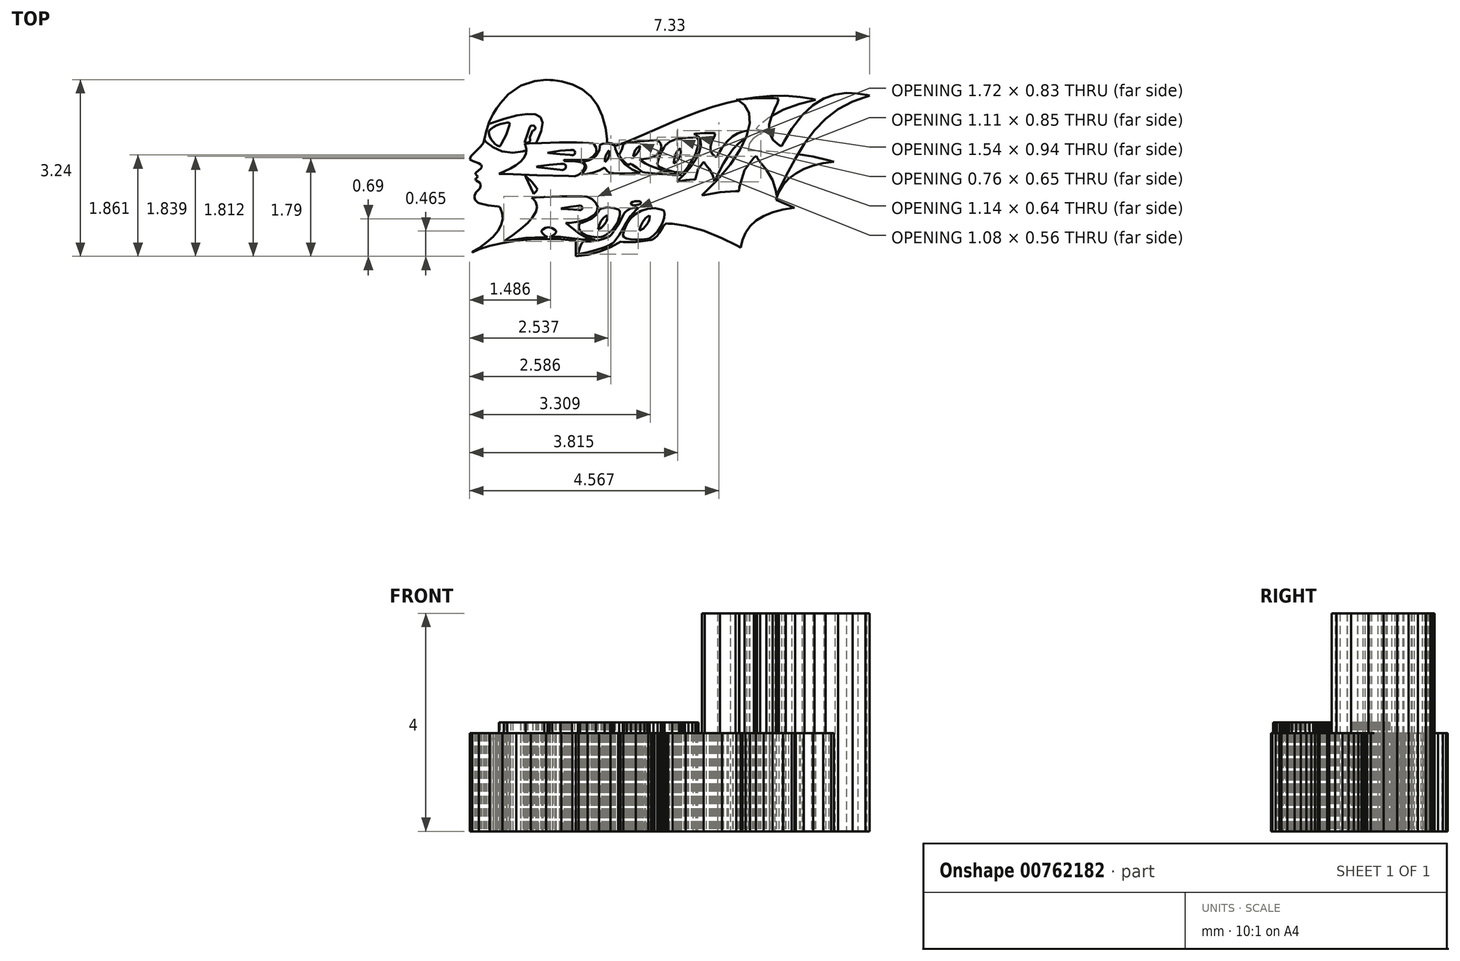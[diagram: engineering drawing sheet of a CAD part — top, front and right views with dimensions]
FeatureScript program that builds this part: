
annotation { "Feature Type Name" : "Feature", "Feature Type Description" : "" }
export const myFeature = defineFeature(function(context is Context, id is Id, definition is map)
    precondition{}
    {
        {
            var Q0;
            Q0=qCreatedBy(makeId("Top.planeOp"),FACE);
            var sketch = newSketch(context, id + "F0", { "sketchPlane" : qUnion([Q0])});
            skLineSegment(sketch, "E0", {"start": v(-3.33, 0.15) * mm, "end": v(-3.34, 0.16) * mm});
            skLineSegment(sketch, "E1", {"start": v(-3.34, 0.16) * mm, "end": v(-3.31, 0.22) * mm});
            skLineSegment(sketch, "E2", {"start": v(-3.31, 0.22) * mm, "end": v(-3.23, 0.3) * mm});
            skLineSegment(sketch, "E3", {"start": v(-3.23, 0.3) * mm, "end": v(-3.14, 0.4) * mm});
            skLineSegment(sketch, "E4", {"start": v(-3.14, 0.4) * mm, "end": v(-3.09, 0.46) * mm});
            skLineSegment(sketch, "E5", {"start": v(-3.09, 0.46) * mm, "end": v(-3.08, 0.48) * mm});
            skLineSegment(sketch, "E6", {"start": v(-3.08, 0.48) * mm, "end": v(-3.07, 0.53) * mm});
            skLineSegment(sketch, "E7", {"start": v(-3.07, 0.53) * mm, "end": v(-3.04, 0.67) * mm});
            skLineSegment(sketch, "E8", {"start": v(-3.04, 0.67) * mm, "end": v(-2.99, 0.84) * mm});
            skLineSegment(sketch, "E9", {"start": v(-2.99, 0.84) * mm, "end": v(-2.91, 1) * mm});
            skLineSegment(sketch, "E10", {"start": v(-2.91, 1) * mm, "end": v(-2.85, 1.1) * mm});
            skLineSegment(sketch, "E11", {"start": v(-2.85, 1.1) * mm, "end": v(-2.82, 1.12) * mm});
            skLineSegment(sketch, "E12", {"start": v(-2.82, 1.12) * mm, "end": v(-2.78, 1.19) * mm});
            skLineSegment(sketch, "E13", {"start": v(-2.78, 1.19) * mm, "end": v(-2.63, 1.35) * mm});
            skLineSegment(sketch, "E14", {"start": v(-2.63, 1.35) * mm, "end": v(-2.4, 1.51) * mm});
            skLineSegment(sketch, "E15", {"start": v(-2.4, 1.51) * mm, "end": v(-2.15, 1.6) * mm});
            skLineSegment(sketch, "E16", {"start": v(-2.15, 1.6) * mm, "end": v(-1.94, 1.62) * mm});
            skLineSegment(sketch, "E17", {"start": v(-1.94, 1.62) * mm, "end": v(-1.87, 1.61) * mm});
            skLineSegment(sketch, "E18", {"start": v(-1.87, 1.61) * mm, "end": v(-1.81, 1.61) * mm});
            skLineSegment(sketch, "E19", {"start": v(-1.81, 1.61) * mm, "end": v(-1.65, 1.6) * mm});
            skLineSegment(sketch, "E20", {"start": v(-1.65, 1.6) * mm, "end": v(-1.45, 1.53) * mm});
            skLineSegment(sketch, "E21", {"start": v(-1.45, 1.53) * mm, "end": v(-1.27, 1.44) * mm});
            skLineSegment(sketch, "E22", {"start": v(-1.27, 1.44) * mm, "end": v(-1.12, 1.32) * mm});
            skLineSegment(sketch, "E23", {"start": v(-1.12, 1.32) * mm, "end": v(-1, 1.15) * mm});
            skLineSegment(sketch, "E24", {"start": v(-1, 1.15) * mm, "end": v(-0.9, 0.96) * mm});
            skLineSegment(sketch, "E25", {"start": v(-0.9, 0.96) * mm, "end": v(-0.85, 0.73) * mm});
            skLineSegment(sketch, "E26", {"start": v(-0.85, 0.73) * mm, "end": v(-0.82, 0.53) * mm});
            skLineSegment(sketch, "E27", {"start": v(-0.82, 0.53) * mm, "end": v(-0.82, 0.46) * mm});
            skLineSegment(sketch, "E28", {"start": v(-0.82, 0.46) * mm, "end": v(-0.8, 0.47) * mm});
            skLineSegment(sketch, "E29", {"start": v(-0.8, 0.47) * mm, "end": v(-0.73, 0.45) * mm});
            skLineSegment(sketch, "E30", {"start": v(-0.73, 0.45) * mm, "end": v(-0.68, 0.42) * mm});
            skLineSegment(sketch, "E31", {"start": v(-0.68, 0.42) * mm, "end": v(-0.67, 0.4) * mm});
            skLineSegment(sketch, "E32", {"start": v(-0.67, 0.4) * mm, "end": v(-0.63, 0.42) * mm});
            skLineSegment(sketch, "E33", {"start": v(-0.63, 0.42) * mm, "end": v(-0.52, 0.46) * mm});
            skLineSegment(sketch, "E34", {"start": v(-0.52, 0.46) * mm, "end": v(-0.36, 0.52) * mm});
            skLineSegment(sketch, "E35", {"start": v(-0.36, 0.52) * mm, "end": v(-0.19, 0.6) * mm});
            skLineSegment(sketch, "E36", {"start": v(-0.19, 0.6) * mm, "end": v(0, 0.68) * mm});
            skLineSegment(sketch, "E37", {"start": v(0, 0.68) * mm, "end": v(0.2, 0.77) * mm});
            skLineSegment(sketch, "E38", {"start": v(0.2, 0.77) * mm, "end": v(0.42, 0.86) * mm});
            skLineSegment(sketch, "E39", {"start": v(0.42, 0.86) * mm, "end": v(0.64, 0.95) * mm});
            skLineSegment(sketch, "E40", {"start": v(0.64, 0.95) * mm, "end": v(0.88, 1.04) * mm});
            skLineSegment(sketch, "E41", {"start": v(0.88, 1.04) * mm, "end": v(1.12, 1.12) * mm});
            skLineSegment(sketch, "E42", {"start": v(1.12, 1.12) * mm, "end": v(1.37, 1.2) * mm});
            skLineSegment(sketch, "E43", {"start": v(1.37, 1.2) * mm, "end": v(1.63, 1.25) * mm});
            skLineSegment(sketch, "E44", {"start": v(1.63, 1.25) * mm, "end": v(1.9, 1.3) * mm});
            skLineSegment(sketch, "E45", {"start": v(1.9, 1.3) * mm, "end": v(2.17, 1.32) * mm});
            skLineSegment(sketch, "E46", {"start": v(2.17, 1.32) * mm, "end": v(2.44, 1.33) * mm});
            skLineSegment(sketch, "E47", {"start": v(2.44, 1.33) * mm, "end": v(2.72, 1.3) * mm});
            skLineSegment(sketch, "E48", {"start": v(2.72, 1.3) * mm, "end": v(2.93, 1.27) * mm});
            skLineSegment(sketch, "E49", {"start": v(2.93, 1.27) * mm, "end": v(3, 1.25) * mm});
            skLineSegment(sketch, "E50", {"start": v(3, 1.25) * mm, "end": v(2.92, 1.23) * mm});
            skLineSegment(sketch, "E51", {"start": v(2.92, 1.23) * mm, "end": v(2.7, 1.18) * mm});
            skLineSegment(sketch, "E52", {"start": v(2.7, 1.18) * mm, "end": v(2.42, 1.07) * mm});
            skLineSegment(sketch, "E53", {"start": v(2.42, 1.07) * mm, "end": v(2.15, 0.93) * mm});
            skLineSegment(sketch, "E54", {"start": v(2.15, 0.93) * mm, "end": v(1.96, 0.77) * mm});
            skLineSegment(sketch, "E55", {"start": v(1.96, 0.77) * mm, "end": v(1.9, 0.72) * mm});
            skLineSegment(sketch, "E56", {"start": v(1.9, 0.72) * mm, "end": v(2.08, 0.68) * mm});
            skLineSegment(sketch, "E57", {"start": v(2.08, 0.68) * mm, "end": v(2.05, 0.66) * mm});
            skLineSegment(sketch, "E58", {"start": v(2.05, 0.66) * mm, "end": v(1.95, 0.6) * mm});
            skLineSegment(sketch, "E59", {"start": v(1.95, 0.6) * mm, "end": v(1.85, 0.54) * mm});
            skLineSegment(sketch, "E60", {"start": v(1.85, 0.54) * mm, "end": v(1.79, 0.45) * mm});
            skLineSegment(sketch, "E61", {"start": v(1.79, 0.45) * mm, "end": v(1.77, 0.36) * mm});
            skLineSegment(sketch, "E62", {"start": v(1.77, 0.36) * mm, "end": v(1.77, 0.32) * mm});
            skLineSegment(sketch, "E63", {"start": v(1.77, 0.32) * mm, "end": v(1.86, 0.32) * mm});
            skLineSegment(sketch, "E64", {"start": v(1.86, 0.32) * mm, "end": v(2.16, 0.31) * mm});
            skLineSegment(sketch, "E65", {"start": v(2.16, 0.31) * mm, "end": v(2.56, 0.27) * mm});
            skLineSegment(sketch, "E66", {"start": v(2.56, 0.27) * mm, "end": v(2.96, 0.2) * mm});
            skLineSegment(sketch, "E67", {"start": v(2.96, 0.2) * mm, "end": v(3.24, 0.14) * mm});
            skLineSegment(sketch, "E68", {"start": v(3.24, 0.14) * mm, "end": v(3.34, 0.11) * mm});
            skLineSegment(sketch, "E69", {"start": v(3.34, 0.11) * mm, "end": v(3.29, 0.1) * mm});
            skLineSegment(sketch, "E70", {"start": v(3.29, 0.1) * mm, "end": v(3.14, 0.09) * mm});
            skLineSegment(sketch, "E71", {"start": v(3.14, 0.09) * mm, "end": v(2.95, 0.04) * mm});
            skLineSegment(sketch, "E72", {"start": v(2.95, 0.04) * mm, "end": v(2.79, -0.02) * mm});
            skLineSegment(sketch, "E73", {"start": v(2.79, -0.02) * mm, "end": v(2.64, -0.1) * mm});
            skLineSegment(sketch, "E74", {"start": v(2.64, -0.1) * mm, "end": v(2.5, -0.2) * mm});
            skLineSegment(sketch, "E75", {"start": v(2.5, -0.2) * mm, "end": v(2.4, -0.31) * mm});
            skLineSegment(sketch, "E76", {"start": v(2.4, -0.31) * mm, "end": v(2.33, -0.44) * mm});
            skLineSegment(sketch, "E77", {"start": v(2.33, -0.44) * mm, "end": v(2.29, -0.55) * mm});
            skLineSegment(sketch, "E78", {"start": v(2.29, -0.55) * mm, "end": v(2.28, -0.59) * mm});
            skLineSegment(sketch, "E79", {"start": v(2.28, -0.59) * mm, "end": v(2.62, -0.73) * mm});
            skLineSegment(sketch, "E80", {"start": v(2.62, -0.73) * mm, "end": v(2.56, -0.74) * mm});
            skLineSegment(sketch, "E81", {"start": v(2.56, -0.74) * mm, "end": v(2.4, -0.76) * mm});
            skLineSegment(sketch, "E82", {"start": v(2.4, -0.76) * mm, "end": v(2.21, -0.81) * mm});
            skLineSegment(sketch, "E83", {"start": v(2.21, -0.81) * mm, "end": v(2.05, -0.88) * mm});
            skLineSegment(sketch, "E84", {"start": v(2.05, -0.88) * mm, "end": v(1.91, -0.97) * mm});
            skLineSegment(sketch, "E85", {"start": v(1.91, -0.97) * mm, "end": v(1.8, -1.07) * mm});
            skLineSegment(sketch, "E86", {"start": v(1.8, -1.07) * mm, "end": v(1.71, -1.19) * mm});
            skLineSegment(sketch, "E87", {"start": v(1.71, -1.19) * mm, "end": v(1.66, -1.32) * mm});
            skLineSegment(sketch, "E88", {"start": v(1.66, -1.32) * mm, "end": v(1.63, -1.43) * mm});
            skLineSegment(sketch, "E89", {"start": v(1.63, -1.43) * mm, "end": v(1.63, -1.46) * mm});
            skLineSegment(sketch, "E90", {"start": v(1.63, -1.46) * mm, "end": v(1.54, -1.42) * mm});
            skLineSegment(sketch, "E91", {"start": v(1.54, -1.42) * mm, "end": v(1.29, -1.29) * mm});
            skLineSegment(sketch, "E92", {"start": v(1.29, -1.29) * mm, "end": v(0.95, -1.15) * mm});
            skLineSegment(sketch, "E93", {"start": v(0.95, -1.15) * mm, "end": v(0.62, -1.06) * mm});
            skLineSegment(sketch, "E94", {"start": v(0.62, -1.06) * mm, "end": v(0.38, -1.02) * mm});
            skLineSegment(sketch, "E95", {"start": v(0.38, -1.02) * mm, "end": v(0.3, -1.02) * mm});
            skLineSegment(sketch, "E96", {"start": v(0.3, -1.02) * mm, "end": v(0.29, -1.02) * mm});
            skLineSegment(sketch, "E97", {"start": v(0.29, -1.02) * mm, "end": v(0.26, -1.02) * mm});
            skLineSegment(sketch, "E98", {"start": v(0.26, -1.02) * mm, "end": v(0.23, -1.05) * mm});
            skLineSegment(sketch, "E99", {"start": v(0.23, -1.05) * mm, "end": v(0.2, -1.09) * mm});
            skLineSegment(sketch, "E100", {"start": v(0.2, -1.09) * mm, "end": v(0.17, -1.14) * mm});
            skLineSegment(sketch, "E101", {"start": v(0.17, -1.14) * mm, "end": v(0.14, -1.19) * mm});
            skLineSegment(sketch, "E102", {"start": v(0.14, -1.19) * mm, "end": v(0.1, -1.24) * mm});
            skLineSegment(sketch, "E103", {"start": v(0.1, -1.24) * mm, "end": v(0.05, -1.29) * mm});
            skLineSegment(sketch, "E104", {"start": v(0.05, -1.29) * mm, "end": v(0, -1.31) * mm});
            skLineSegment(sketch, "E105", {"start": v(0, -1.31) * mm, "end": v(-0.01, -1.32) * mm});
            skLineSegment(sketch, "E106", {"start": v(-0.01, -1.32) * mm, "end": v(-0.07, -1.33) * mm});
            skLineSegment(sketch, "E107", {"start": v(-0.07, -1.33) * mm, "end": v(-0.3, -1.36) * mm});
            skLineSegment(sketch, "E108", {"start": v(-0.3, -1.36) * mm, "end": v(-0.52, -1.36) * mm});
            skLineSegment(sketch, "E109", {"start": v(-0.52, -1.36) * mm, "end": v(-0.57, -1.35) * mm});
            skLineSegment(sketch, "E110", {"start": v(-0.57, -1.35) * mm, "end": v(-0.62, -1.38) * mm});
            skLineSegment(sketch, "E111", {"start": v(-0.62, -1.38) * mm, "end": v(-0.76, -1.45) * mm});
            skLineSegment(sketch, "E112", {"start": v(-0.76, -1.45) * mm, "end": v(-0.97, -1.53) * mm});
            skLineSegment(sketch, "E113", {"start": v(-0.97, -1.53) * mm, "end": v(-1.18, -1.6) * mm});
            skLineSegment(sketch, "E114", {"start": v(-1.18, -1.6) * mm, "end": v(-1.34, -1.62) * mm});
            skLineSegment(sketch, "E115", {"start": v(-1.34, -1.62) * mm, "end": v(-1.4, -1.62) * mm});
            skLineSegment(sketch, "E116", {"start": v(-1.4, -1.62) * mm, "end": v(-1.4, -1.34) * mm});
            skLineSegment(sketch, "E117", {"start": v(-1.4, -1.34) * mm, "end": v(-1.46, -1.33) * mm});
            skLineSegment(sketch, "E118", {"start": v(-1.46, -1.33) * mm, "end": v(-1.66, -1.3) * mm});
            skLineSegment(sketch, "E119", {"start": v(-1.66, -1.3) * mm, "end": v(-1.94, -1.3) * mm});
            skLineSegment(sketch, "E120", {"start": v(-1.94, -1.3) * mm, "end": v(-2.22, -1.3) * mm});
            skLineSegment(sketch, "E121", {"start": v(-2.22, -1.3) * mm, "end": v(-2.49, -1.33) * mm});
            skLineSegment(sketch, "E122", {"start": v(-2.49, -1.33) * mm, "end": v(-2.74, -1.38) * mm});
            skLineSegment(sketch, "E123", {"start": v(-2.74, -1.38) * mm, "end": v(-2.97, -1.43) * mm});
            skLineSegment(sketch, "E124", {"start": v(-2.97, -1.43) * mm, "end": v(-3.17, -1.5) * mm});
            skLineSegment(sketch, "E125", {"start": v(-3.17, -1.5) * mm, "end": v(-3.3, -1.55) * mm});
            skLineSegment(sketch, "E126", {"start": v(-3.3, -1.55) * mm, "end": v(-3.33, -1.57) * mm});
            skLineSegment(sketch, "E127", {"start": v(-3.33, -1.57) * mm, "end": v(-3.3, -1.55) * mm});
            skLineSegment(sketch, "E128", {"start": v(-3.3, -1.55) * mm, "end": v(-3.17, -1.47) * mm});
            skLineSegment(sketch, "E129", {"start": v(-3.17, -1.47) * mm, "end": v(-3.03, -1.37) * mm});
            skLineSegment(sketch, "E130", {"start": v(-3.03, -1.37) * mm, "end": v(-2.91, -1.26) * mm});
            skLineSegment(sketch, "E131", {"start": v(-2.91, -1.26) * mm, "end": v(-2.82, -1.15) * mm});
            skLineSegment(sketch, "E132", {"start": v(-2.82, -1.15) * mm, "end": v(-2.76, -1.05) * mm});
            skLineSegment(sketch, "E133", {"start": v(-2.76, -1.05) * mm, "end": v(-2.74, -0.93) * mm});
            skLineSegment(sketch, "E134", {"start": v(-2.74, -0.93) * mm, "end": v(-2.75, -0.82) * mm});
            skLineSegment(sketch, "E135", {"start": v(-2.75, -0.82) * mm, "end": v(-2.78, -0.74) * mm});
            skLineSegment(sketch, "E136", {"start": v(-2.78, -0.74) * mm, "end": v(-2.8, -0.7) * mm});
            skLineSegment(sketch, "E137", {"start": v(-2.8, -0.7) * mm, "end": v(-2.83, -0.7) * mm});
            skLineSegment(sketch, "E138", {"start": v(-2.83, -0.7) * mm, "end": v(-3, -0.69) * mm});
            skLineSegment(sketch, "E139", {"start": v(-3, -0.69) * mm, "end": v(-3.16, -0.65) * mm});
            skLineSegment(sketch, "E140", {"start": v(-3.16, -0.65) * mm, "end": v(-3.2, -0.63) * mm});
            skLineSegment(sketch, "E141", {"start": v(-3.2, -0.63) * mm, "end": v(-3.2, -0.62) * mm});
            skLineSegment(sketch, "E142", {"start": v(-3.2, -0.62) * mm, "end": v(-3.24, -0.58) * mm});
            skLineSegment(sketch, "E143", {"start": v(-3.24, -0.58) * mm, "end": v(-3.25, -0.52) * mm});
            skLineSegment(sketch, "E144", {"start": v(-3.25, -0.52) * mm, "end": v(-3.23, -0.45) * mm});
            skLineSegment(sketch, "E145", {"start": v(-3.23, -0.45) * mm, "end": v(-3.18, -0.4) * mm});
            skLineSegment(sketch, "E146", {"start": v(-3.18, -0.4) * mm, "end": v(-3.16, -0.38) * mm});
            skLineSegment(sketch, "E147", {"start": v(-3.16, -0.38) * mm, "end": v(-3.16, -0.37) * mm});
            skLineSegment(sketch, "E148", {"start": v(-3.16, -0.37) * mm, "end": v(-3.14, -0.33) * mm});
            skLineSegment(sketch, "E149", {"start": v(-3.14, -0.33) * mm, "end": v(-3.15, -0.28) * mm});
            skLineSegment(sketch, "E150", {"start": v(-3.15, -0.28) * mm, "end": v(-3.15, -0.27) * mm});
            skLineSegment(sketch, "E151", {"start": v(-3.15, -0.27) * mm, "end": v(-3.16, -0.27) * mm});
            skLineSegment(sketch, "E152", {"start": v(-3.16, -0.27) * mm, "end": v(-3.22, -0.23) * mm});
            skLineSegment(sketch, "E153", {"start": v(-3.22, -0.23) * mm, "end": v(-3.23, -0.23) * mm});
            skLineSegment(sketch, "E154", {"start": v(-3.23, -0.23) * mm, "end": v(-3.23, -0.22) * mm});
            skLineSegment(sketch, "E155", {"start": v(-3.23, -0.22) * mm, "end": v(-3.24, -0.2) * mm});
            skLineSegment(sketch, "E156", {"start": v(-3.24, -0.2) * mm, "end": v(-3.23, -0.2) * mm});
            skLineSegment(sketch, "E157", {"start": v(-3.23, -0.2) * mm, "end": v(-3.23, -0.19) * mm});
            skLineSegment(sketch, "E158", {"start": v(-3.23, -0.19) * mm, "end": v(-3.22, -0.19) * mm});
            skLineSegment(sketch, "E159", {"start": v(-3.22, -0.19) * mm, "end": v(-3.2, -0.18) * mm});
            skLineSegment(sketch, "E160", {"start": v(-3.2, -0.18) * mm, "end": v(-3.2, -0.16) * mm});
            skLineSegment(sketch, "E161", {"start": v(-3.2, -0.16) * mm, "end": v(-3.2, -0.14) * mm});
            skLineSegment(sketch, "E162", {"start": v(-3.2, -0.14) * mm, "end": v(-3.22, -0.12) * mm});
            skLineSegment(sketch, "E163", {"start": v(-3.22, -0.12) * mm, "end": v(-3.23, -0.12) * mm});
            skLineSegment(sketch, "E164", {"start": v(-3.23, -0.12) * mm, "end": v(-3.23, -0.12) * mm});
            skLineSegment(sketch, "E165", {"start": v(-3.23, -0.12) * mm, "end": v(-3.23, -0.1) * mm});
            skLineSegment(sketch, "E166", {"start": v(-3.23, -0.1) * mm, "end": v(-3.23, -0.09) * mm});
            skLineSegment(sketch, "E167", {"start": v(-3.23, -0.09) * mm, "end": v(-3.14, 0) * mm});
            skLineSegment(sketch, "E168", {"start": v(-3.14, 0) * mm, "end": v(-3.13, 0) * mm});
            skLineSegment(sketch, "E169", {"start": v(-3.13, 0) * mm, "end": v(-3.12, 0.01) * mm});
            skLineSegment(sketch, "E170", {"start": v(-3.12, 0.01) * mm, "end": v(-3.12, 0.04) * mm});
            skLineSegment(sketch, "E171", {"start": v(-3.12, 0.04) * mm, "end": v(-3.13, 0.05) * mm});
            skLineSegment(sketch, "E172", {"start": v(-3.13, 0.05) * mm, "end": v(-3.13, 0.06) * mm});
            skLineSegment(sketch, "E173", {"start": v(-3.13, 0.06) * mm, "end": v(-3.13, 0.06) * mm});
            skLineSegment(sketch, "E174", {"start": v(-3.13, 0.06) * mm, "end": v(-3.14, 0.07) * mm});
            skLineSegment(sketch, "E175", {"start": v(-3.14, 0.07) * mm, "end": v(-3.18, 0.1) * mm});
            skLineSegment(sketch, "E176", {"start": v(-3.18, 0.1) * mm, "end": v(-3.23, 0.11) * mm});
            skLineSegment(sketch, "E177", {"start": v(-3.23, 0.11) * mm, "end": v(-3.28, 0.13) * mm});
            skLineSegment(sketch, "E178", {"start": v(-3.28, 0.13) * mm, "end": v(-3.32, 0.15) * mm});
            skLineSegment(sketch, "E179", {"start": v(-3.32, 0.15) * mm, "end": v(-3.33, 0.15) * mm});
            skLineSegment(sketch, "E180", {"start": v(-2.33, 0.45) * mm, "end": v(-2.26, 0.45) * mm});
            skLineSegment(sketch, "E181", {"start": v(-2.26, 0.45) * mm, "end": v(-2.02, 0.46) * mm});
            skLineSegment(sketch, "E182", {"start": v(-2.02, 0.46) * mm, "end": v(-1.7, 0.47) * mm});
            skLineSegment(sketch, "E183", {"start": v(-1.7, 0.47) * mm, "end": v(-1.38, 0.47) * mm});
            skLineSegment(sketch, "E184", {"start": v(-1.38, 0.47) * mm, "end": v(-1.15, 0.46) * mm});
            skLineSegment(sketch, "E185", {"start": v(-1.15, 0.46) * mm, "end": v(-1.07, 0.45) * mm});
            skLineSegment(sketch, "E186", {"start": v(-1.07, 0.45) * mm, "end": v(-1.06, 0.43) * mm});
            skLineSegment(sketch, "E187", {"start": v(-1.06, 0.43) * mm, "end": v(-1.02, 0.37) * mm});
            skLineSegment(sketch, "E188", {"start": v(-1.02, 0.37) * mm, "end": v(-1.02, 0.29) * mm});
            skLineSegment(sketch, "E189", {"start": v(-1.02, 0.29) * mm, "end": v(-1.07, 0.21) * mm});
            skLineSegment(sketch, "E190", {"start": v(-1.07, 0.21) * mm, "end": v(-1.16, 0.16) * mm});
            skLineSegment(sketch, "E191", {"start": v(-1.16, 0.16) * mm, "end": v(-1.2, 0.15) * mm});
            skLineSegment(sketch, "E192", {"start": v(-1.2, 0.15) * mm, "end": v(-1.23, 0.15) * mm});
            skLineSegment(sketch, "E193", {"start": v(-1.23, 0.15) * mm, "end": v(-1.57, 0.15) * mm});
            skLineSegment(sketch, "E194", {"start": v(-1.57, 0.15) * mm, "end": v(-1.6, 0.15) * mm});
            skLineSegment(sketch, "E195", {"start": v(-1.6, 0.15) * mm, "end": v(-1.6, 0.15) * mm});
            skLineSegment(sketch, "E196", {"start": v(-1.6, 0.15) * mm, "end": v(-1.61, 0.13) * mm});
            skLineSegment(sketch, "E197", {"start": v(-1.61, 0.13) * mm, "end": v(-1.6, 0.13) * mm});
            skLineSegment(sketch, "E198", {"start": v(-1.6, 0.13) * mm, "end": v(-1.6, 0.13) * mm});
            skLineSegment(sketch, "E199", {"start": v(-1.6, 0.13) * mm, "end": v(-1.57, 0.13) * mm});
            skLineSegment(sketch, "E200", {"start": v(-1.57, 0.13) * mm, "end": v(-1.5, 0.13) * mm});
            skLineSegment(sketch, "E201", {"start": v(-1.5, 0.13) * mm, "end": v(-1.4, 0.12) * mm});
            skLineSegment(sketch, "E202", {"start": v(-1.4, 0.12) * mm, "end": v(-1.32, 0.11) * mm});
            skLineSegment(sketch, "E203", {"start": v(-1.32, 0.11) * mm, "end": v(-1.28, 0.1) * mm});
            skLineSegment(sketch, "E204", {"start": v(-1.28, 0.1) * mm, "end": v(-1.27, 0.1) * mm});
            skLineSegment(sketch, "E205", {"start": v(-1.27, 0.1) * mm, "end": v(-1.26, 0.09) * mm});
            skLineSegment(sketch, "E206", {"start": v(-1.26, 0.09) * mm, "end": v(-1.24, 0.07) * mm});
            skLineSegment(sketch, "E207", {"start": v(-1.24, 0.07) * mm, "end": v(-1.23, 0.04) * mm});
            skLineSegment(sketch, "E208", {"start": v(-1.23, 0.04) * mm, "end": v(-1.23, 0) * mm});
            skLineSegment(sketch, "E209", {"start": v(-1.23, 0) * mm, "end": v(-1.25, -0.03) * mm});
            skLineSegment(sketch, "E210", {"start": v(-1.25, -0.03) * mm, "end": v(-1.28, -0.07) * mm});
            skLineSegment(sketch, "E211", {"start": v(-1.28, -0.07) * mm, "end": v(-1.32, -0.1) * mm});
            skLineSegment(sketch, "E212", {"start": v(-1.32, -0.1) * mm, "end": v(-1.36, -0.13) * mm});
            skLineSegment(sketch, "E213", {"start": v(-1.36, -0.13) * mm, "end": v(-1.4, -0.15) * mm});
            skLineSegment(sketch, "E214", {"start": v(-1.4, -0.15) * mm, "end": v(-1.4, -0.15) * mm});
            skLineSegment(sketch, "E215", {"start": v(-1.4, -0.15) * mm, "end": v(-1.53, -0.15) * mm});
            skLineSegment(sketch, "E216", {"start": v(-1.53, -0.15) * mm, "end": v(-2.1, -0.13) * mm});
            skLineSegment(sketch, "E217", {"start": v(-2.1, -0.13) * mm, "end": v(-2.69, -0.1) * mm});
            skLineSegment(sketch, "E218", {"start": v(-2.69, -0.1) * mm, "end": v(-2.8, -0.1) * mm});
            skLineSegment(sketch, "E219", {"start": v(-2.8, -0.1) * mm, "end": v(-2.78, -0.1) * mm});
            skLineSegment(sketch, "E220", {"start": v(-2.78, -0.1) * mm, "end": v(-2.7, -0.06) * mm});
            skLineSegment(sketch, "E221", {"start": v(-2.7, -0.06) * mm, "end": v(-2.59, 0) * mm});
            skLineSegment(sketch, "E222", {"start": v(-2.59, 0) * mm, "end": v(-2.5, 0.05) * mm});
            skLineSegment(sketch, "E223", {"start": v(-2.5, 0.05) * mm, "end": v(-2.4, 0.12) * mm});
            skLineSegment(sketch, "E224", {"start": v(-2.4, 0.12) * mm, "end": v(-2.34, 0.19) * mm});
            skLineSegment(sketch, "E225", {"start": v(-2.34, 0.19) * mm, "end": v(-2.3, 0.27) * mm});
            skLineSegment(sketch, "E226", {"start": v(-2.3, 0.27) * mm, "end": v(-2.3, 0.35) * mm});
            skLineSegment(sketch, "E227", {"start": v(-2.3, 0.35) * mm, "end": v(-2.32, 0.43) * mm});
            skLineSegment(sketch, "E228", {"start": v(-2.32, 0.43) * mm, "end": v(-2.33, 0.45) * mm});
            skLineSegment(sketch, "E229", {"start": v(-1.91, 0.28) * mm, "end": v(-1.88, 0.29) * mm});
            skLineSegment(sketch, "E230", {"start": v(-1.88, 0.29) * mm, "end": v(-1.68, 0.32) * mm});
            skLineSegment(sketch, "E231", {"start": v(-1.68, 0.32) * mm, "end": v(-1.49, 0.33) * mm});
            skLineSegment(sketch, "E232", {"start": v(-1.49, 0.33) * mm, "end": v(-1.45, 0.33) * mm});
            skLineSegment(sketch, "E233", {"start": v(-1.45, 0.33) * mm, "end": v(-1.44, 0.33) * mm});
            skLineSegment(sketch, "E234", {"start": v(-1.44, 0.33) * mm, "end": v(-1.42, 0.32) * mm});
            skLineSegment(sketch, "E235", {"start": v(-1.42, 0.32) * mm, "end": v(-1.4, 0.28) * mm});
            skLineSegment(sketch, "E236", {"start": v(-1.4, 0.28) * mm, "end": v(-1.42, 0.25) * mm});
            skLineSegment(sketch, "E237", {"start": v(-1.42, 0.25) * mm, "end": v(-1.45, 0.24) * mm});
            skLineSegment(sketch, "E238", {"start": v(-1.45, 0.24) * mm, "end": v(-1.46, 0.24) * mm});
            skLineSegment(sketch, "E239", {"start": v(-1.46, 0.24) * mm, "end": v(-1.5, 0.24) * mm});
            skLineSegment(sketch, "E240", {"start": v(-1.5, 0.24) * mm, "end": v(-1.69, 0.25) * mm});
            skLineSegment(sketch, "E241", {"start": v(-1.69, 0.25) * mm, "end": v(-1.87, 0.27) * mm});
            skLineSegment(sketch, "E242", {"start": v(-1.87, 0.27) * mm, "end": v(-1.91, 0.28) * mm});
            skLineSegment(sketch, "E243", {"start": v(-1.26, 0.12) * mm, "end": v(-1.25, 0.11) * mm});
            skLineSegment(sketch, "E244", {"start": v(-1.25, 0.11) * mm, "end": v(-1.22, 0.07) * mm});
            skLineSegment(sketch, "E245", {"start": v(-1.22, 0.07) * mm, "end": v(-1.2, 0.02) * mm});
            skLineSegment(sketch, "E246", {"start": v(-1.2, 0.02) * mm, "end": v(-1.23, -0.04) * mm});
            skLineSegment(sketch, "E247", {"start": v(-1.23, -0.04) * mm, "end": v(-1.27, -0.1) * mm});
            skLineSegment(sketch, "E248", {"start": v(-1.27, -0.1) * mm, "end": v(-1.3, -0.11) * mm});
            skLineSegment(sketch, "E249", {"start": v(-1.3, -0.11) * mm, "end": v(-1.26, -0.11) * mm});
            skLineSegment(sketch, "E250", {"start": v(-1.26, -0.11) * mm, "end": v(-1.18, -0.1) * mm});
            skLineSegment(sketch, "E251", {"start": v(-1.18, -0.1) * mm, "end": v(-1.07, -0.08) * mm});
            skLineSegment(sketch, "E252", {"start": v(-1.07, -0.08) * mm, "end": v(-0.96, -0.04) * mm});
            skLineSegment(sketch, "E253", {"start": v(-0.96, -0.04) * mm, "end": v(-0.89, 0) * mm});
            skLineSegment(sketch, "E254", {"start": v(-0.89, 0) * mm, "end": v(-0.87, 0.01) * mm});
            skLineSegment(sketch, "E255", {"start": v(-0.87, 0.01) * mm, "end": v(-0.86, 0) * mm});
            skLineSegment(sketch, "E256", {"start": v(-0.86, 0) * mm, "end": v(-0.84, -0.03) * mm});
            skLineSegment(sketch, "E257", {"start": v(-0.84, -0.03) * mm, "end": v(-0.82, -0.06) * mm});
            skLineSegment(sketch, "E258", {"start": v(-0.82, -0.06) * mm, "end": v(-0.78, -0.08) * mm});
            skLineSegment(sketch, "E259", {"start": v(-0.78, -0.08) * mm, "end": v(-0.75, -0.09) * mm});
            skLineSegment(sketch, "E260", {"start": v(-0.75, -0.09) * mm, "end": v(-0.74, -0.09) * mm});
            skLineSegment(sketch, "E261", {"start": v(-0.74, -0.09) * mm, "end": v(-0.7, -0.1) * mm});
            skLineSegment(sketch, "E262", {"start": v(-0.7, -0.1) * mm, "end": v(-0.48, -0.1) * mm});
            skLineSegment(sketch, "E263", {"start": v(-0.48, -0.1) * mm, "end": v(-0.26, -0.1) * mm});
            skLineSegment(sketch, "E264", {"start": v(-0.26, -0.1) * mm, "end": v(-0.22, -0.09) * mm});
            skLineSegment(sketch, "E265", {"start": v(-0.22, -0.09) * mm, "end": v(-0.25, -0.07) * mm});
            skLineSegment(sketch, "E266", {"start": v(-0.25, -0.07) * mm, "end": v(-0.36, -0.02) * mm});
            skLineSegment(sketch, "E267", {"start": v(-0.36, -0.02) * mm, "end": v(-0.5, 0.07) * mm});
            skLineSegment(sketch, "E268", {"start": v(-0.5, 0.07) * mm, "end": v(-0.6, 0.2) * mm});
            skLineSegment(sketch, "E269", {"start": v(-0.6, 0.2) * mm, "end": v(-0.67, 0.35) * mm});
            skLineSegment(sketch, "E270", {"start": v(-0.67, 0.35) * mm, "end": v(-0.68, 0.4) * mm});
            skLineSegment(sketch, "E271", {"start": v(-0.68, 0.4) * mm, "end": v(-0.69, 0.41) * mm});
            skLineSegment(sketch, "E272", {"start": v(-0.69, 0.41) * mm, "end": v(-0.74, 0.44) * mm});
            skLineSegment(sketch, "E273", {"start": v(-0.74, 0.44) * mm, "end": v(-0.82, 0.45) * mm});
            skLineSegment(sketch, "E274", {"start": v(-0.82, 0.45) * mm, "end": v(-0.9, 0.44) * mm});
            skLineSegment(sketch, "E275", {"start": v(-0.9, 0.44) * mm, "end": v(-0.95, 0.43) * mm});
            skLineSegment(sketch, "E276", {"start": v(-0.95, 0.43) * mm, "end": v(-0.96, 0.42) * mm});
            skLineSegment(sketch, "E277", {"start": v(-0.96, 0.42) * mm, "end": v(-0.96, 0.41) * mm});
            skLineSegment(sketch, "E278", {"start": v(-0.96, 0.41) * mm, "end": v(-0.96, 0.38) * mm});
            skLineSegment(sketch, "E279", {"start": v(-0.96, 0.38) * mm, "end": v(-0.96, 0.34) * mm});
            skLineSegment(sketch, "E280", {"start": v(-0.96, 0.34) * mm, "end": v(-0.99, 0.28) * mm});
            skLineSegment(sketch, "E281", {"start": v(-0.99, 0.28) * mm, "end": v(-1.02, 0.23) * mm});
            skLineSegment(sketch, "E282", {"start": v(-1.02, 0.23) * mm, "end": v(-1.08, 0.18) * mm});
            skLineSegment(sketch, "E283", {"start": v(-1.08, 0.18) * mm, "end": v(-1.16, 0.14) * mm});
            skLineSegment(sketch, "E284", {"start": v(-1.16, 0.14) * mm, "end": v(-1.24, 0.12) * mm});
            skLineSegment(sketch, "E285", {"start": v(-1.24, 0.12) * mm, "end": v(-1.26, 0.12) * mm});
            skLineSegment(sketch, "E286", {"start": v(-0.78, 0.32) * mm, "end": v(-0.8, 0.31) * mm});
            skLineSegment(sketch, "E287", {"start": v(-0.8, 0.31) * mm, "end": v(-0.82, 0.28) * mm});
            skLineSegment(sketch, "E288", {"start": v(-0.82, 0.28) * mm, "end": v(-0.85, 0.22) * mm});
            skLineSegment(sketch, "E289", {"start": v(-0.85, 0.22) * mm, "end": v(-0.86, 0.17) * mm});
            skLineSegment(sketch, "E290", {"start": v(-0.86, 0.17) * mm, "end": v(-0.86, 0.13) * mm});
            skLineSegment(sketch, "E291", {"start": v(-0.86, 0.13) * mm, "end": v(-0.86, 0.11) * mm});
            skLineSegment(sketch, "E292", {"start": v(-0.86, 0.11) * mm, "end": v(-0.85, 0.12) * mm});
            skLineSegment(sketch, "E293", {"start": v(-0.85, 0.12) * mm, "end": v(-0.82, 0.15) * mm});
            skLineSegment(sketch, "E294", {"start": v(-0.82, 0.15) * mm, "end": v(-0.79, 0.2) * mm});
            skLineSegment(sketch, "E295", {"start": v(-0.79, 0.2) * mm, "end": v(-0.77, 0.27) * mm});
            skLineSegment(sketch, "E296", {"start": v(-0.77, 0.27) * mm, "end": v(-0.78, 0.3) * mm});
            skLineSegment(sketch, "E297", {"start": v(-0.78, 0.3) * mm, "end": v(-0.78, 0.32) * mm});
            skLineSegment(sketch, "E298", {"start": v(-0.6, 0.24) * mm, "end": v(-0.6, 0.22) * mm});
            skLineSegment(sketch, "E299", {"start": v(-0.6, 0.22) * mm, "end": v(-0.54, 0.14) * mm});
            skLineSegment(sketch, "E300", {"start": v(-0.54, 0.14) * mm, "end": v(-0.47, 0.08) * mm});
            skLineSegment(sketch, "E301", {"start": v(-0.47, 0.08) * mm, "end": v(-0.45, 0.06) * mm});
            skLineSegment(sketch, "E302", {"start": v(-0.45, 0.06) * mm, "end": v(-0.44, 0.06) * mm});
            skLineSegment(sketch, "E303", {"start": v(-0.44, 0.06) * mm, "end": v(-0.41, 0.06) * mm});
            skLineSegment(sketch, "E304", {"start": v(-0.41, 0.06) * mm, "end": v(-0.4, 0.07) * mm});
            skLineSegment(sketch, "E305", {"start": v(-0.4, 0.07) * mm, "end": v(-0.39, 0.08) * mm});
            skLineSegment(sketch, "E306", {"start": v(-0.39, 0.08) * mm, "end": v(-0.37, 0.07) * mm});
            skLineSegment(sketch, "E307", {"start": v(-0.37, 0.07) * mm, "end": v(-0.27, 0) * mm});
            skLineSegment(sketch, "E308", {"start": v(-0.27, 0) * mm, "end": v(-0.19, -0.06) * mm});
            skLineSegment(sketch, "E309", {"start": v(-0.19, -0.06) * mm, "end": v(-0.17, -0.08) * mm});
            skLineSegment(sketch, "E310", {"start": v(-0.17, -0.08) * mm, "end": v(-0.13, -0.08) * mm});
            skLineSegment(sketch, "E311", {"start": v(-0.13, -0.08) * mm, "end": v(0, -0.1) * mm});
            skLineSegment(sketch, "E312", {"start": v(0, -0.1) * mm, "end": v(0.19, -0.11) * mm});
            skLineSegment(sketch, "E313", {"start": v(0.19, -0.11) * mm, "end": v(0.37, -0.12) * mm});
            skLineSegment(sketch, "E314", {"start": v(0.37, -0.12) * mm, "end": v(0.5, -0.13) * mm});
            skLineSegment(sketch, "E315", {"start": v(0.5, -0.13) * mm, "end": v(0.54, -0.13) * mm});
            skLineSegment(sketch, "E316", {"start": v(0.54, -0.13) * mm, "end": v(0.51, -0.12) * mm});
            skLineSegment(sketch, "E317", {"start": v(0.51, -0.12) * mm, "end": v(0.43, -0.1) * mm});
            skLineSegment(sketch, "E318", {"start": v(0.43, -0.1) * mm, "end": v(0.32, -0.08) * mm});
            skLineSegment(sketch, "E319", {"start": v(0.32, -0.08) * mm, "end": v(0.2, -0.04) * mm});
            skLineSegment(sketch, "E320", {"start": v(0.2, -0.04) * mm, "end": v(0.08, 0) * mm});
            skLineSegment(sketch, "E321", {"start": v(0.08, 0) * mm, "end": v(-0.03, 0.04) * mm});
            skLineSegment(sketch, "E322", {"start": v(-0.03, 0.04) * mm, "end": v(-0.12, 0.08) * mm});
            skLineSegment(sketch, "E323", {"start": v(-0.12, 0.08) * mm, "end": v(-0.19, 0.13) * mm});
            skLineSegment(sketch, "E324", {"start": v(-0.19, 0.13) * mm, "end": v(-0.22, 0.15) * mm});
            skLineSegment(sketch, "E325", {"start": v(-0.22, 0.15) * mm, "end": v(-0.23, 0.16) * mm});
            skLineSegment(sketch, "E326", {"start": v(-0.23, 0.16) * mm, "end": v(-0.19, 0.16) * mm});
            skLineSegment(sketch, "E327", {"start": v(-0.19, 0.16) * mm, "end": v(-0.07, 0.18) * mm});
            skLineSegment(sketch, "E328", {"start": v(-0.07, 0.18) * mm, "end": v(0.04, 0.21) * mm});
            skLineSegment(sketch, "E329", {"start": v(0.04, 0.21) * mm, "end": v(0.12, 0.27) * mm});
            skLineSegment(sketch, "E330", {"start": v(0.12, 0.27) * mm, "end": v(0.16, 0.33) * mm});
            skLineSegment(sketch, "E331", {"start": v(0.16, 0.33) * mm, "end": v(0.17, 0.39) * mm});
            skLineSegment(sketch, "E332", {"start": v(0.17, 0.39) * mm, "end": v(0.16, 0.45) * mm});
            skLineSegment(sketch, "E333", {"start": v(0.16, 0.45) * mm, "end": v(0.13, 0.49) * mm});
            skLineSegment(sketch, "E334", {"start": v(0.13, 0.49) * mm, "end": v(0.1, 0.5) * mm});
            skLineSegment(sketch, "E335", {"start": v(0.1, 0.5) * mm, "end": v(0.09, 0.51) * mm});
            skLineSegment(sketch, "E336", {"start": v(0.09, 0.51) * mm, "end": v(0.04, 0.51) * mm});
            skLineSegment(sketch, "E337", {"start": v(0.04, 0.51) * mm, "end": v(-0.22, 0.5) * mm});
            skLineSegment(sketch, "E338", {"start": v(-0.22, 0.5) * mm, "end": v(-0.47, 0.46) * mm});
            skLineSegment(sketch, "E339", {"start": v(-0.47, 0.46) * mm, "end": v(-0.52, 0.45) * mm});
            skLineSegment(sketch, "E340", {"start": v(-0.52, 0.45) * mm, "end": v(-0.53, 0.43) * mm});
            skLineSegment(sketch, "E341", {"start": v(-0.53, 0.43) * mm, "end": v(-0.55, 0.34) * mm});
            skLineSegment(sketch, "E342", {"start": v(-0.55, 0.34) * mm, "end": v(-0.6, 0.26) * mm});
            skLineSegment(sketch, "E343", {"start": v(-0.6, 0.26) * mm, "end": v(-0.6, 0.24) * mm});
            skLineSegment(sketch, "E344", {"start": v(0.23, 0.4) * mm, "end": v(0.22, 0.37) * mm});
            skLineSegment(sketch, "E345", {"start": v(0.22, 0.37) * mm, "end": v(0.18, 0.3) * mm});
            skLineSegment(sketch, "E346", {"start": v(0.18, 0.3) * mm, "end": v(0.14, 0.22) * mm});
            skLineSegment(sketch, "E347", {"start": v(0.14, 0.22) * mm, "end": v(0.12, 0.15) * mm});
            skLineSegment(sketch, "E348", {"start": v(0.12, 0.15) * mm, "end": v(0.1, 0.1) * mm});
            skLineSegment(sketch, "E349", {"start": v(0.1, 0.1) * mm, "end": v(0.1, 0.08) * mm});
            skLineSegment(sketch, "E350", {"start": v(0.1, 0.08) * mm, "end": v(0.1, 0.07) * mm});
            skLineSegment(sketch, "E351", {"start": v(0.1, 0.07) * mm, "end": v(0.13, 0.03) * mm});
            skLineSegment(sketch, "E352", {"start": v(0.13, 0.03) * mm, "end": v(0.25, -0.03) * mm});
            skLineSegment(sketch, "E353", {"start": v(0.25, -0.03) * mm, "end": v(0.4, -0.07) * mm});
            skLineSegment(sketch, "E354", {"start": v(0.4, -0.07) * mm, "end": v(0.54, -0.08) * mm});
            skLineSegment(sketch, "E355", {"start": v(0.54, -0.08) * mm, "end": v(0.58, -0.08) * mm});
            skLineSegment(sketch, "E356", {"start": v(0.58, -0.08) * mm, "end": v(0.6, -0.05) * mm});
            skLineSegment(sketch, "E357", {"start": v(0.6, -0.05) * mm, "end": v(0.67, 0.03) * mm});
            skLineSegment(sketch, "E358", {"start": v(0.67, 0.03) * mm, "end": v(0.74, 0.14) * mm});
            skLineSegment(sketch, "E359", {"start": v(0.74, 0.14) * mm, "end": v(0.8, 0.25) * mm});
            skLineSegment(sketch, "E360", {"start": v(0.8, 0.25) * mm, "end": v(0.83, 0.35) * mm});
            skLineSegment(sketch, "E361", {"start": v(0.83, 0.35) * mm, "end": v(0.85, 0.44) * mm});
            skLineSegment(sketch, "E362", {"start": v(0.85, 0.44) * mm, "end": v(0.85, 0.5) * mm});
            skLineSegment(sketch, "E363", {"start": v(0.85, 0.5) * mm, "end": v(0.84, 0.55) * mm});
            skLineSegment(sketch, "E364", {"start": v(0.84, 0.55) * mm, "end": v(0.81, 0.56) * mm});
            skLineSegment(sketch, "E365", {"start": v(0.81, 0.56) * mm, "end": v(0.8, 0.56) * mm});
            skLineSegment(sketch, "E366", {"start": v(0.8, 0.56) * mm, "end": v(0.76, 0.56) * mm});
            skLineSegment(sketch, "E367", {"start": v(0.76, 0.56) * mm, "end": v(0.62, 0.55) * mm});
            skLineSegment(sketch, "E368", {"start": v(0.62, 0.55) * mm, "end": v(0.46, 0.53) * mm});
            skLineSegment(sketch, "E369", {"start": v(0.46, 0.53) * mm, "end": v(0.32, 0.48) * mm});
            skLineSegment(sketch, "E370", {"start": v(0.32, 0.48) * mm, "end": v(0.25, 0.42) * mm});
            skLineSegment(sketch, "E371", {"start": v(0.25, 0.42) * mm, "end": v(0.23, 0.4) * mm});
            skLineSegment(sketch, "E372", {"start": v(0.77, 0.63) * mm, "end": v(0.8, 0.62) * mm});
            skLineSegment(sketch, "E373", {"start": v(0.8, 0.62) * mm, "end": v(0.85, 0.58) * mm});
            skLineSegment(sketch, "E374", {"start": v(0.85, 0.58) * mm, "end": v(0.9, 0.5) * mm});
            skLineSegment(sketch, "E375", {"start": v(0.9, 0.5) * mm, "end": v(0.9, 0.4) * mm});
            skLineSegment(sketch, "E376", {"start": v(0.9, 0.4) * mm, "end": v(0.87, 0.3) * mm});
            skLineSegment(sketch, "E377", {"start": v(0.87, 0.3) * mm, "end": v(0.8, 0.17) * mm});
            skLineSegment(sketch, "E378", {"start": v(0.8, 0.17) * mm, "end": v(0.72, 0.03) * mm});
            skLineSegment(sketch, "E379", {"start": v(0.72, 0.03) * mm, "end": v(0.6, -0.1) * mm});
            skLineSegment(sketch, "E380", {"start": v(0.6, -0.1) * mm, "end": v(0.5, -0.22) * mm});
            skLineSegment(sketch, "E381", {"start": v(0.5, -0.22) * mm, "end": v(0.46, -0.25) * mm});
            skLineSegment(sketch, "E382", {"start": v(0.46, -0.25) * mm, "end": v(0.49, -0.25) * mm});
            skLineSegment(sketch, "E383", {"start": v(0.49, -0.25) * mm, "end": v(0.62, -0.22) * mm});
            skLineSegment(sketch, "E384", {"start": v(0.62, -0.22) * mm, "end": v(0.77, -0.21) * mm});
            skLineSegment(sketch, "E385", {"start": v(0.77, -0.21) * mm, "end": v(0.8, -0.21) * mm});
            skLineSegment(sketch, "E386", {"start": v(0.8, -0.21) * mm, "end": v(0.8, -0.18) * mm});
            skLineSegment(sketch, "E387", {"start": v(0.8, -0.18) * mm, "end": v(0.85, -0.02) * mm});
            skLineSegment(sketch, "E388", {"start": v(0.85, -0.02) * mm, "end": v(0.94, 0.1) * mm});
            skLineSegment(sketch, "E389", {"start": v(0.94, 0.1) * mm, "end": v(0.96, 0.11) * mm});
            skLineSegment(sketch, "E390", {"start": v(0.96, 0.11) * mm, "end": v(0.96, 0.1) * mm});
            skLineSegment(sketch, "E391", {"start": v(0.96, 0.1) * mm, "end": v(1, 0.05) * mm});
            skLineSegment(sketch, "E392", {"start": v(1, 0.05) * mm, "end": v(1.05, -0.02) * mm});
            skLineSegment(sketch, "E393", {"start": v(1.05, -0.02) * mm, "end": v(1.1, -0.11) * mm});
            skLineSegment(sketch, "E394", {"start": v(1.1, -0.11) * mm, "end": v(1.14, -0.22) * mm});
            skLineSegment(sketch, "E395", {"start": v(1.14, -0.22) * mm, "end": v(1.14, -0.25) * mm});
            skLineSegment(sketch, "E396", {"start": v(1.14, -0.25) * mm, "end": v(1.16, -0.2) * mm});
            skLineSegment(sketch, "E397", {"start": v(1.16, -0.2) * mm, "end": v(1.23, -0.07) * mm});
            skLineSegment(sketch, "E398", {"start": v(1.23, -0.07) * mm, "end": v(1.31, 0.08) * mm});
            skLineSegment(sketch, "E399", {"start": v(1.31, 0.08) * mm, "end": v(1.4, 0.22) * mm});
            skLineSegment(sketch, "E400", {"start": v(1.4, 0.22) * mm, "end": v(1.49, 0.35) * mm});
            skLineSegment(sketch, "E401", {"start": v(1.49, 0.35) * mm, "end": v(1.6, 0.45) * mm});
            skLineSegment(sketch, "E402", {"start": v(1.6, 0.45) * mm, "end": v(1.7, 0.54) * mm});
            skLineSegment(sketch, "E403", {"start": v(1.7, 0.54) * mm, "end": v(1.84, 0.6) * mm});
            skLineSegment(sketch, "E404", {"start": v(1.84, 0.6) * mm, "end": v(1.96, 0.65) * mm});
            skLineSegment(sketch, "E405", {"start": v(1.96, 0.65) * mm, "end": v(2, 0.66) * mm});
            skLineSegment(sketch, "E406", {"start": v(2, 0.66) * mm, "end": v(1.97, 0.67) * mm});
            skLineSegment(sketch, "E407", {"start": v(1.97, 0.67) * mm, "end": v(1.89, 0.68) * mm});
            skLineSegment(sketch, "E408", {"start": v(1.89, 0.68) * mm, "end": v(1.78, 0.69) * mm});
            skLineSegment(sketch, "E409", {"start": v(1.78, 0.69) * mm, "end": v(1.68, 0.67) * mm});
            skLineSegment(sketch, "E410", {"start": v(1.68, 0.67) * mm, "end": v(1.58, 0.64) * mm});
            skLineSegment(sketch, "E411", {"start": v(1.58, 0.64) * mm, "end": v(1.47, 0.58) * mm});
            skLineSegment(sketch, "E412", {"start": v(1.47, 0.58) * mm, "end": v(1.38, 0.48) * mm});
            skLineSegment(sketch, "E413", {"start": v(1.38, 0.48) * mm, "end": v(1.28, 0.36) * mm});
            skLineSegment(sketch, "E414", {"start": v(1.28, 0.36) * mm, "end": v(1.21, 0.24) * mm});
            skLineSegment(sketch, "E415", {"start": v(1.21, 0.24) * mm, "end": v(1.19, 0.2) * mm});
            skLineSegment(sketch, "E416", {"start": v(1.19, 0.2) * mm, "end": v(1.17, 0.21) * mm});
            skLineSegment(sketch, "E417", {"start": v(1.17, 0.21) * mm, "end": v(1.11, 0.26) * mm});
            skLineSegment(sketch, "E418", {"start": v(1.11, 0.26) * mm, "end": v(1.08, 0.32) * mm});
            skLineSegment(sketch, "E419", {"start": v(1.08, 0.32) * mm, "end": v(1.08, 0.4) * mm});
            skLineSegment(sketch, "E420", {"start": v(1.08, 0.4) * mm, "end": v(1.1, 0.47) * mm});
            skLineSegment(sketch, "E421", {"start": v(1.1, 0.47) * mm, "end": v(1.13, 0.54) * mm});
            skLineSegment(sketch, "E422", {"start": v(1.13, 0.54) * mm, "end": v(1.15, 0.6) * mm});
            skLineSegment(sketch, "E423", {"start": v(1.15, 0.6) * mm, "end": v(1.16, 0.63) * mm});
            skLineSegment(sketch, "E424", {"start": v(1.16, 0.63) * mm, "end": v(1.15, 0.64) * mm});
            skLineSegment(sketch, "E425", {"start": v(1.15, 0.64) * mm, "end": v(1.14, 0.64) * mm});
            skLineSegment(sketch, "E426", {"start": v(1.14, 0.64) * mm, "end": v(1.11, 0.64) * mm});
            skLineSegment(sketch, "E427", {"start": v(1.11, 0.64) * mm, "end": v(0.96, 0.64) * mm});
            skLineSegment(sketch, "E428", {"start": v(0.96, 0.64) * mm, "end": v(0.8, 0.63) * mm});
            skLineSegment(sketch, "E429", {"start": v(0.8, 0.63) * mm, "end": v(0.77, 0.63) * mm});
            skLineSegment(sketch, "E430", {"start": v(-2.2, -0.54) * mm, "end": v(-2.12, -0.54) * mm});
            skLineSegment(sketch, "E431", {"start": v(-2.12, -0.54) * mm, "end": v(-1.7, -0.52) * mm});
            skLineSegment(sketch, "E432", {"start": v(-1.7, -0.52) * mm, "end": v(-1.27, -0.52) * mm});
            skLineSegment(sketch, "E433", {"start": v(-1.27, -0.52) * mm, "end": v(-1.2, -0.53) * mm});
            skLineSegment(sketch, "E434", {"start": v(-1.2, -0.53) * mm, "end": v(-1.17, -0.53) * mm});
            skLineSegment(sketch, "E435", {"start": v(-1.17, -0.53) * mm, "end": v(-1.1, -0.57) * mm});
            skLineSegment(sketch, "E436", {"start": v(-1.1, -0.57) * mm, "end": v(-1.03, -0.63) * mm});
            skLineSegment(sketch, "E437", {"start": v(-1.03, -0.63) * mm, "end": v(-1, -0.7) * mm});
            skLineSegment(sketch, "E438", {"start": v(-1, -0.7) * mm, "end": v(-1, -0.79) * mm});
            skLineSegment(sketch, "E439", {"start": v(-1, -0.79) * mm, "end": v(-1.06, -0.86) * mm});
            skLineSegment(sketch, "E440", {"start": v(-1.06, -0.86) * mm, "end": v(-1.17, -0.93) * mm});
            skLineSegment(sketch, "E441", {"start": v(-1.17, -0.93) * mm, "end": v(-1.34, -0.98) * mm});
            skLineSegment(sketch, "E442", {"start": v(-1.34, -0.98) * mm, "end": v(-1.52, -1) * mm});
            skLineSegment(sketch, "E443", {"start": v(-1.52, -1) * mm, "end": v(-1.58, -1) * mm});
            skLineSegment(sketch, "E444", {"start": v(-1.58, -1) * mm, "end": v(-1.55, -1.03) * mm});
            skLineSegment(sketch, "E445", {"start": v(-1.55, -1.03) * mm, "end": v(-1.46, -1.1) * mm});
            skLineSegment(sketch, "E446", {"start": v(-1.46, -1.1) * mm, "end": v(-1.34, -1.2) * mm});
            skLineSegment(sketch, "E447", {"start": v(-1.34, -1.2) * mm, "end": v(-1.2, -1.27) * mm});
            skLineSegment(sketch, "E448", {"start": v(-1.2, -1.27) * mm, "end": v(-1.08, -1.3) * mm});
            skLineSegment(sketch, "E449", {"start": v(-1.08, -1.3) * mm, "end": v(-1.04, -1.31) * mm});
            skLineSegment(sketch, "E450", {"start": v(-1.04, -1.31) * mm, "end": v(-1.09, -1.32) * mm});
            skLineSegment(sketch, "E451", {"start": v(-1.09, -1.32) * mm, "end": v(-1.25, -1.31) * mm});
            skLineSegment(sketch, "E452", {"start": v(-1.25, -1.31) * mm, "end": v(-1.46, -1.29) * mm});
            skLineSegment(sketch, "E453", {"start": v(-1.46, -1.29) * mm, "end": v(-1.68, -1.26) * mm});
            skLineSegment(sketch, "E454", {"start": v(-1.68, -1.26) * mm, "end": v(-1.83, -1.26) * mm});
            skLineSegment(sketch, "E455", {"start": v(-1.83, -1.26) * mm, "end": v(-1.87, -1.27) * mm});
            skLineSegment(sketch, "E456", {"start": v(-1.87, -1.27) * mm, "end": v(-1.86, -1.27) * mm});
            skLineSegment(sketch, "E457", {"start": v(-1.86, -1.27) * mm, "end": v(-1.82, -1.25) * mm});
            skLineSegment(sketch, "E458", {"start": v(-1.82, -1.25) * mm, "end": v(-1.78, -1.21) * mm});
            skLineSegment(sketch, "E459", {"start": v(-1.78, -1.21) * mm, "end": v(-1.75, -1.18) * mm});
            skLineSegment(sketch, "E460", {"start": v(-1.75, -1.18) * mm, "end": v(-1.75, -1.15) * mm});
            skLineSegment(sketch, "E461", {"start": v(-1.75, -1.15) * mm, "end": v(-1.76, -1.15) * mm});
            skLineSegment(sketch, "E462", {"start": v(-1.76, -1.15) * mm, "end": v(-1.77, -1.13) * mm});
            skLineSegment(sketch, "E463", {"start": v(-1.77, -1.13) * mm, "end": v(-1.82, -1.1) * mm});
            skLineSegment(sketch, "E464", {"start": v(-1.82, -1.1) * mm, "end": v(-1.89, -1.09) * mm});
            skLineSegment(sketch, "E465", {"start": v(-1.89, -1.09) * mm, "end": v(-1.95, -1.1) * mm});
            skLineSegment(sketch, "E466", {"start": v(-1.95, -1.1) * mm, "end": v(-2, -1.13) * mm});
            skLineSegment(sketch, "E467", {"start": v(-2, -1.13) * mm, "end": v(-2.02, -1.14) * mm});
            skLineSegment(sketch, "E468", {"start": v(-2.02, -1.14) * mm, "end": v(-2.02, -1.15) * mm});
            skLineSegment(sketch, "E469", {"start": v(-2.02, -1.15) * mm, "end": v(-2.02, -1.17) * mm});
            skLineSegment(sketch, "E470", {"start": v(-2.02, -1.17) * mm, "end": v(-2, -1.2) * mm});
            skLineSegment(sketch, "E471", {"start": v(-2, -1.2) * mm, "end": v(-1.96, -1.24) * mm});
            skLineSegment(sketch, "E472", {"start": v(-1.96, -1.24) * mm, "end": v(-1.92, -1.26) * mm});
            skLineSegment(sketch, "E473", {"start": v(-1.92, -1.26) * mm, "end": v(-1.91, -1.27) * mm});
            skLineSegment(sketch, "E474", {"start": v(-1.91, -1.27) * mm, "end": v(-1.97, -1.27) * mm});
            skLineSegment(sketch, "E475", {"start": v(-1.97, -1.27) * mm, "end": v(-2.31, -1.28) * mm});
            skLineSegment(sketch, "E476", {"start": v(-2.31, -1.28) * mm, "end": v(-2.65, -1.33) * mm});
            skLineSegment(sketch, "E477", {"start": v(-2.65, -1.33) * mm, "end": v(-2.71, -1.34) * mm});
            skLineSegment(sketch, "E478", {"start": v(-2.71, -1.34) * mm, "end": v(-2.67, -1.32) * mm});
            skLineSegment(sketch, "E479", {"start": v(-2.67, -1.32) * mm, "end": v(-2.55, -1.23) * mm});
            skLineSegment(sketch, "E480", {"start": v(-2.55, -1.23) * mm, "end": v(-2.4, -1.12) * mm});
            skLineSegment(sketch, "E481", {"start": v(-2.4, -1.12) * mm, "end": v(-2.28, -1) * mm});
            skLineSegment(sketch, "E482", {"start": v(-2.28, -1) * mm, "end": v(-2.18, -0.9) * mm});
            skLineSegment(sketch, "E483", {"start": v(-2.18, -0.9) * mm, "end": v(-2.13, -0.8) * mm});
            skLineSegment(sketch, "E484", {"start": v(-2.13, -0.8) * mm, "end": v(-2.1, -0.7) * mm});
            skLineSegment(sketch, "E485", {"start": v(-2.1, -0.7) * mm, "end": v(-2.13, -0.62) * mm});
            skLineSegment(sketch, "E486", {"start": v(-2.13, -0.62) * mm, "end": v(-2.18, -0.56) * mm});
            skLineSegment(sketch, "E487", {"start": v(-2.18, -0.56) * mm, "end": v(-2.2, -0.54) * mm});
            skLineSegment(sketch, "E488", {"start": v(-1.3, -1) * mm, "end": v(-1.28, -1) * mm});
            skLineSegment(sketch, "E489", {"start": v(-1.28, -1) * mm, "end": v(-1.2, -0.97) * mm});
            skLineSegment(sketch, "E490", {"start": v(-1.2, -0.97) * mm, "end": v(-1.1, -0.92) * mm});
            skLineSegment(sketch, "E491", {"start": v(-1.1, -0.92) * mm, "end": v(-1.02, -0.86) * mm});
            skLineSegment(sketch, "E492", {"start": v(-1.02, -0.86) * mm, "end": v(-0.98, -0.8) * mm});
            skLineSegment(sketch, "E493", {"start": v(-0.98, -0.8) * mm, "end": v(-0.97, -0.79) * mm});
            skLineSegment(sketch, "E494", {"start": v(-0.97, -0.79) * mm, "end": v(-0.97, -0.77) * mm});
            skLineSegment(sketch, "E495", {"start": v(-0.97, -0.77) * mm, "end": v(-0.92, -0.74) * mm});
            skLineSegment(sketch, "E496", {"start": v(-0.92, -0.74) * mm, "end": v(-0.82, -0.72) * mm});
            skLineSegment(sketch, "E497", {"start": v(-0.82, -0.72) * mm, "end": v(-0.7, -0.74) * mm});
            skLineSegment(sketch, "E498", {"start": v(-0.7, -0.74) * mm, "end": v(-0.61, -0.76) * mm});
            skLineSegment(sketch, "E499", {"start": v(-0.61, -0.76) * mm, "end": v(-0.6, -0.78) * mm});
            skLineSegment(sketch, "E500", {"start": v(-0.6, -0.78) * mm, "end": v(-0.58, -0.8) * mm});
            skLineSegment(sketch, "E501", {"start": v(-0.58, -0.8) * mm, "end": v(-0.59, -0.86) * mm});
            skLineSegment(sketch, "E502", {"start": v(-0.59, -0.86) * mm, "end": v(-0.62, -1) * mm});
            skLineSegment(sketch, "E503", {"start": v(-0.62, -1) * mm, "end": v(-0.72, -1.13) * mm});
            skLineSegment(sketch, "E504", {"start": v(-0.72, -1.13) * mm, "end": v(-0.85, -1.23) * mm});
            skLineSegment(sketch, "E505", {"start": v(-0.85, -1.23) * mm, "end": v(-0.9, -1.26) * mm});
            skLineSegment(sketch, "E506", {"start": v(-0.9, -1.26) * mm, "end": v(-0.92, -1.26) * mm});
            skLineSegment(sketch, "E507", {"start": v(-0.92, -1.26) * mm, "end": v(-1.01, -1.27) * mm});
            skLineSegment(sketch, "E508", {"start": v(-1.01, -1.27) * mm, "end": v(-1.11, -1.26) * mm});
            skLineSegment(sketch, "E509", {"start": v(-1.11, -1.26) * mm, "end": v(-1.2, -1.23) * mm});
            skLineSegment(sketch, "E510", {"start": v(-1.2, -1.23) * mm, "end": v(-1.27, -1.2) * mm});
            skLineSegment(sketch, "E511", {"start": v(-1.27, -1.2) * mm, "end": v(-1.31, -1.15) * mm});
            skLineSegment(sketch, "E512", {"start": v(-1.31, -1.15) * mm, "end": v(-1.34, -1.1) * mm});
            skLineSegment(sketch, "E513", {"start": v(-1.34, -1.1) * mm, "end": v(-1.34, -1.05) * mm});
            skLineSegment(sketch, "E514", {"start": v(-1.34, -1.05) * mm, "end": v(-1.32, -1.02) * mm});
            skLineSegment(sketch, "E515", {"start": v(-1.32, -1.02) * mm, "end": v(-1.3, -1) * mm});
            skLineSegment(sketch, "E516", {"start": v(-1.25, -1.34) * mm, "end": v(-1.26, -1.35) * mm});
            skLineSegment(sketch, "E517", {"start": v(-1.26, -1.35) * mm, "end": v(-1.3, -1.4) * mm});
            skLineSegment(sketch, "E518", {"start": v(-1.3, -1.4) * mm, "end": v(-1.32, -1.45) * mm});
            skLineSegment(sketch, "E519", {"start": v(-1.32, -1.45) * mm, "end": v(-1.34, -1.52) * mm});
            skLineSegment(sketch, "E520", {"start": v(-1.34, -1.52) * mm, "end": v(-1.35, -1.57) * mm});
            skLineSegment(sketch, "E521", {"start": v(-1.35, -1.57) * mm, "end": v(-1.36, -1.58) * mm});
            skLineSegment(sketch, "E522", {"start": v(-1.36, -1.58) * mm, "end": v(-1.31, -1.57) * mm});
            skLineSegment(sketch, "E523", {"start": v(-1.31, -1.57) * mm, "end": v(-1.2, -1.55) * mm});
            skLineSegment(sketch, "E524", {"start": v(-1.2, -1.55) * mm, "end": v(-1.02, -1.5) * mm});
            skLineSegment(sketch, "E525", {"start": v(-1.02, -1.5) * mm, "end": v(-0.87, -1.46) * mm});
            skLineSegment(sketch, "E526", {"start": v(-0.87, -1.46) * mm, "end": v(-0.76, -1.41) * mm});
            skLineSegment(sketch, "E527", {"start": v(-0.76, -1.41) * mm, "end": v(-0.73, -1.4) * mm});
            skLineSegment(sketch, "E528", {"start": v(-0.73, -1.4) * mm, "end": v(-0.7, -1.36) * mm});
            skLineSegment(sketch, "E529", {"start": v(-0.7, -1.36) * mm, "end": v(-0.6, -1.23) * mm});
            skLineSegment(sketch, "E530", {"start": v(-0.6, -1.23) * mm, "end": v(-0.5, -1.05) * mm});
            skLineSegment(sketch, "E531", {"start": v(-0.5, -1.05) * mm, "end": v(-0.4, -0.88) * mm});
            skLineSegment(sketch, "E532", {"start": v(-0.4, -0.88) * mm, "end": v(-0.3, -0.77) * mm});
            skLineSegment(sketch, "E533", {"start": v(-0.3, -0.77) * mm, "end": v(-0.25, -0.74) * mm});
            skLineSegment(sketch, "E534", {"start": v(-0.25, -0.74) * mm, "end": v(-0.27, -0.73) * mm});
            skLineSegment(sketch, "E535", {"start": v(-0.27, -0.73) * mm, "end": v(-0.33, -0.73) * mm});
            skLineSegment(sketch, "E536", {"start": v(-0.33, -0.73) * mm, "end": v(-0.39, -0.74) * mm});
            skLineSegment(sketch, "E537", {"start": v(-0.39, -0.74) * mm, "end": v(-0.45, -0.77) * mm});
            skLineSegment(sketch, "E538", {"start": v(-0.45, -0.77) * mm, "end": v(-0.5, -0.81) * mm});
            skLineSegment(sketch, "E539", {"start": v(-0.5, -0.81) * mm, "end": v(-0.5, -0.83) * mm});
            skLineSegment(sketch, "E540", {"start": v(-0.5, -0.83) * mm, "end": v(-0.52, -0.86) * mm});
            skLineSegment(sketch, "E541", {"start": v(-0.52, -0.86) * mm, "end": v(-0.62, -1.05) * mm});
            skLineSegment(sketch, "E542", {"start": v(-0.62, -1.05) * mm, "end": v(-0.74, -1.22) * mm});
            skLineSegment(sketch, "E543", {"start": v(-0.74, -1.22) * mm, "end": v(-0.77, -1.25) * mm});
            skLineSegment(sketch, "E544", {"start": v(-0.77, -1.25) * mm, "end": v(-0.8, -1.26) * mm});
            skLineSegment(sketch, "E545", {"start": v(-0.8, -1.26) * mm, "end": v(-0.87, -1.3) * mm});
            skLineSegment(sketch, "E546", {"start": v(-0.87, -1.3) * mm, "end": v(-0.98, -1.33) * mm});
            skLineSegment(sketch, "E547", {"start": v(-0.98, -1.33) * mm, "end": v(-1.1, -1.35) * mm});
            skLineSegment(sketch, "E548", {"start": v(-1.1, -1.35) * mm, "end": v(-1.21, -1.34) * mm});
            skLineSegment(sketch, "E549", {"start": v(-1.21, -1.34) * mm, "end": v(-1.25, -1.34) * mm});
            skLineSegment(sketch, "E550", {"start": v(-2.12, 0.02) * mm, "end": v(-2.08, 0.03) * mm});
            skLineSegment(sketch, "E551", {"start": v(-2.08, 0.03) * mm, "end": v(-1.88, 0.06) * mm});
            skLineSegment(sketch, "E552", {"start": v(-1.88, 0.06) * mm, "end": v(-1.68, 0.07) * mm});
            skLineSegment(sketch, "E553", {"start": v(-1.68, 0.07) * mm, "end": v(-1.64, 0.08) * mm});
            skLineSegment(sketch, "E554", {"start": v(-1.64, 0.08) * mm, "end": v(-1.63, 0.08) * mm});
            skLineSegment(sketch, "E555", {"start": v(-1.63, 0.08) * mm, "end": v(-1.6, 0.07) * mm});
            skLineSegment(sketch, "E556", {"start": v(-1.6, 0.07) * mm, "end": v(-1.59, 0.06) * mm});
            skLineSegment(sketch, "E557", {"start": v(-1.59, 0.06) * mm, "end": v(-1.58, 0.04) * mm});
            skLineSegment(sketch, "E558", {"start": v(-1.58, 0.04) * mm, "end": v(-1.58, 0.02) * mm});
            skLineSegment(sketch, "E559", {"start": v(-1.58, 0.02) * mm, "end": v(-1.58, 0) * mm});
            skLineSegment(sketch, "E560", {"start": v(-1.58, 0) * mm, "end": v(-1.6, -0.02) * mm});
            skLineSegment(sketch, "E561", {"start": v(-1.6, -0.02) * mm, "end": v(-1.62, -0.03) * mm});
            skLineSegment(sketch, "E562", {"start": v(-1.62, -0.03) * mm, "end": v(-1.64, -0.04) * mm});
            skLineSegment(sketch, "E563", {"start": v(-1.64, -0.04) * mm, "end": v(-1.65, -0.03) * mm});
            skLineSegment(sketch, "E564", {"start": v(-1.65, -0.03) * mm, "end": v(-1.69, -0.03) * mm});
            skLineSegment(sketch, "E565", {"start": v(-1.69, -0.03) * mm, "end": v(-2.08, 0.01) * mm});
            skLineSegment(sketch, "E566", {"start": v(-2.08, 0.01) * mm, "end": v(-2.12, 0.02) * mm});
            skLineSegment(sketch, "E567", {"start": v(-0.22, 0.4) * mm, "end": v(-0.24, 0.4) * mm});
            skLineSegment(sketch, "E568", {"start": v(-0.24, 0.4) * mm, "end": v(-0.27, 0.37) * mm});
            skLineSegment(sketch, "E569", {"start": v(-0.27, 0.37) * mm, "end": v(-0.3, 0.32) * mm});
            skLineSegment(sketch, "E570", {"start": v(-0.3, 0.32) * mm, "end": v(-0.33, 0.27) * mm});
            skLineSegment(sketch, "E571", {"start": v(-0.33, 0.27) * mm, "end": v(-0.34, 0.23) * mm});
            skLineSegment(sketch, "E572", {"start": v(-0.34, 0.23) * mm, "end": v(-0.34, 0.22) * mm});
            skLineSegment(sketch, "E573", {"start": v(-0.34, 0.22) * mm, "end": v(-0.33, 0.22) * mm});
            skLineSegment(sketch, "E574", {"start": v(-0.33, 0.22) * mm, "end": v(-0.3, 0.24) * mm});
            skLineSegment(sketch, "E575", {"start": v(-0.3, 0.24) * mm, "end": v(-0.25, 0.3) * mm});
            skLineSegment(sketch, "E576", {"start": v(-0.25, 0.3) * mm, "end": v(-0.23, 0.35) * mm});
            skLineSegment(sketch, "E577", {"start": v(-0.23, 0.35) * mm, "end": v(-0.22, 0.4) * mm});
            skLineSegment(sketch, "E578", {"start": v(-0.22, 0.4) * mm, "end": v(-0.22, 0.4) * mm});
            skLineSegment(sketch, "E579", {"start": v(0.52, 0.36) * mm, "end": v(0.5, 0.35) * mm});
            skLineSegment(sketch, "E580", {"start": v(0.5, 0.35) * mm, "end": v(0.46, 0.3) * mm});
            skLineSegment(sketch, "E581", {"start": v(0.46, 0.3) * mm, "end": v(0.43, 0.24) * mm});
            skLineSegment(sketch, "E582", {"start": v(0.43, 0.24) * mm, "end": v(0.41, 0.16) * mm});
            skLineSegment(sketch, "E583", {"start": v(0.41, 0.16) * mm, "end": v(0.4, 0.1) * mm});
            skLineSegment(sketch, "E584", {"start": v(0.4, 0.1) * mm, "end": v(0.4, 0.08) * mm});
            skLineSegment(sketch, "E585", {"start": v(0.4, 0.08) * mm, "end": v(0.41, 0.09) * mm});
            skLineSegment(sketch, "E586", {"start": v(0.41, 0.09) * mm, "end": v(0.43, 0.1) * mm});
            skLineSegment(sketch, "E587", {"start": v(0.43, 0.1) * mm, "end": v(0.46, 0.13) * mm});
            skLineSegment(sketch, "E588", {"start": v(0.46, 0.13) * mm, "end": v(0.49, 0.16) * mm});
            skLineSegment(sketch, "E589", {"start": v(0.49, 0.16) * mm, "end": v(0.5, 0.2) * mm});
            skLineSegment(sketch, "E590", {"start": v(0.5, 0.2) * mm, "end": v(0.52, 0.25) * mm});
            skLineSegment(sketch, "E591", {"start": v(0.52, 0.25) * mm, "end": v(0.53, 0.29) * mm});
            skLineSegment(sketch, "E592", {"start": v(0.53, 0.29) * mm, "end": v(0.53, 0.33) * mm});
            skLineSegment(sketch, "E593", {"start": v(0.53, 0.33) * mm, "end": v(0.53, 0.36) * mm});
            skLineSegment(sketch, "E594", {"start": v(0.53, 0.36) * mm, "end": v(0.52, 0.36) * mm});
            skLineSegment(sketch, "E595", {"start": v(-1.67, -0.75) * mm, "end": v(-1.64, -0.74) * mm});
            skLineSegment(sketch, "E596", {"start": v(-1.64, -0.74) * mm, "end": v(-1.49, -0.7) * mm});
            skLineSegment(sketch, "E597", {"start": v(-1.49, -0.7) * mm, "end": v(-1.34, -0.7) * mm});
            skLineSegment(sketch, "E598", {"start": v(-1.34, -0.7) * mm, "end": v(-1.3, -0.69) * mm});
            skLineSegment(sketch, "E599", {"start": v(-1.3, -0.69) * mm, "end": v(-1.3, -0.69) * mm});
            skLineSegment(sketch, "E600", {"start": v(-1.3, -0.69) * mm, "end": v(-1.28, -0.7) * mm});
            skLineSegment(sketch, "E601", {"start": v(-1.28, -0.7) * mm, "end": v(-1.28, -0.73) * mm});
            skLineSegment(sketch, "E602", {"start": v(-1.28, -0.73) * mm, "end": v(-1.28, -0.76) * mm});
            skLineSegment(sketch, "E603", {"start": v(-1.28, -0.76) * mm, "end": v(-1.3, -0.77) * mm});
            skLineSegment(sketch, "E604", {"start": v(-1.3, -0.77) * mm, "end": v(-1.31, -0.77) * mm});
            skLineSegment(sketch, "E605", {"start": v(-1.31, -0.77) * mm, "end": v(-1.34, -0.77) * mm});
            skLineSegment(sketch, "E606", {"start": v(-1.34, -0.77) * mm, "end": v(-1.64, -0.75) * mm});
            skLineSegment(sketch, "E607", {"start": v(-1.64, -0.75) * mm, "end": v(-1.67, -0.75) * mm});
            skLineSegment(sketch, "E608", {"start": v(-0.82, -0.87) * mm, "end": v(-0.84, -0.88) * mm});
            skLineSegment(sketch, "E609", {"start": v(-0.84, -0.88) * mm, "end": v(-0.89, -0.91) * mm});
            skLineSegment(sketch, "E610", {"start": v(-0.89, -0.91) * mm, "end": v(-0.94, -0.98) * mm});
            skLineSegment(sketch, "E611", {"start": v(-0.94, -0.98) * mm, "end": v(-0.97, -1.05) * mm});
            skLineSegment(sketch, "E612", {"start": v(-0.97, -1.05) * mm, "end": v(-0.98, -1.1) * mm});
            skLineSegment(sketch, "E613", {"start": v(-0.98, -1.1) * mm, "end": v(-0.99, -1.13) * mm});
            skLineSegment(sketch, "E614", {"start": v(-0.99, -1.13) * mm, "end": v(-0.98, -1.12) * mm});
            skLineSegment(sketch, "E615", {"start": v(-0.98, -1.12) * mm, "end": v(-0.95, -1.11) * mm});
            skLineSegment(sketch, "E616", {"start": v(-0.95, -1.11) * mm, "end": v(-0.92, -1.1) * mm});
            skLineSegment(sketch, "E617", {"start": v(-0.92, -1.1) * mm, "end": v(-0.89, -1.06) * mm});
            skLineSegment(sketch, "E618", {"start": v(-0.89, -1.06) * mm, "end": v(-0.86, -1.02) * mm});
            skLineSegment(sketch, "E619", {"start": v(-0.86, -1.02) * mm, "end": v(-0.84, -0.99) * mm});
            skLineSegment(sketch, "E620", {"start": v(-0.84, -0.99) * mm, "end": v(-0.82, -0.95) * mm});
            skLineSegment(sketch, "E621", {"start": v(-0.82, -0.95) * mm, "end": v(-0.81, -0.9) * mm});
            skLineSegment(sketch, "E622", {"start": v(-0.81, -0.9) * mm, "end": v(-0.81, -0.88) * mm});
            skLineSegment(sketch, "E623", {"start": v(-0.81, -0.88) * mm, "end": v(-0.82, -0.87) * mm});
            skLineSegment(sketch, "E624", {"start": v(-0.3, -0.6) * mm, "end": v(-0.29, -0.6) * mm});
            skLineSegment(sketch, "E625", {"start": v(-0.29, -0.6) * mm, "end": v(-0.26, -0.6) * mm});
            skLineSegment(sketch, "E626", {"start": v(-0.26, -0.6) * mm, "end": v(-0.23, -0.61) * mm});
            skLineSegment(sketch, "E627", {"start": v(-0.23, -0.61) * mm, "end": v(-0.2, -0.62) * mm});
            skLineSegment(sketch, "E628", {"start": v(-0.2, -0.62) * mm, "end": v(-0.2, -0.63) * mm});
            skLineSegment(sketch, "E629", {"start": v(-0.2, -0.63) * mm, "end": v(-0.2, -0.63) * mm});
            skLineSegment(sketch, "E630", {"start": v(-0.2, -0.63) * mm, "end": v(-0.2, -0.64) * mm});
            skLineSegment(sketch, "E631", {"start": v(-0.2, -0.64) * mm, "end": v(-0.21, -0.66) * mm});
            skLineSegment(sketch, "E632", {"start": v(-0.21, -0.66) * mm, "end": v(-0.25, -0.68) * mm});
            skLineSegment(sketch, "E633", {"start": v(-0.25, -0.68) * mm, "end": v(-0.3, -0.68) * mm});
            skLineSegment(sketch, "E634", {"start": v(-0.3, -0.68) * mm, "end": v(-0.34, -0.68) * mm});
            skLineSegment(sketch, "E635", {"start": v(-0.34, -0.68) * mm, "end": v(-0.36, -0.68) * mm});
            skLineSegment(sketch, "E636", {"start": v(-0.36, -0.68) * mm, "end": v(-0.36, -0.68) * mm});
            skLineSegment(sketch, "E637", {"start": v(-0.36, -0.68) * mm, "end": v(-0.38, -0.66) * mm});
            skLineSegment(sketch, "E638", {"start": v(-0.38, -0.66) * mm, "end": v(-0.38, -0.64) * mm});
            skLineSegment(sketch, "E639", {"start": v(-0.38, -0.64) * mm, "end": v(-0.35, -0.62) * mm});
            skLineSegment(sketch, "E640", {"start": v(-0.35, -0.62) * mm, "end": v(-0.31, -0.6) * mm});
            skLineSegment(sketch, "E641", {"start": v(-0.31, -0.6) * mm, "end": v(-0.3, -0.6) * mm});
            skLineSegment(sketch, "E642", {"start": v(-0.53, -1.23) * mm, "end": v(-0.53, -1.2) * mm});
            skLineSegment(sketch, "E643", {"start": v(-0.53, -1.2) * mm, "end": v(-0.5, -1.13) * mm});
            skLineSegment(sketch, "E644", {"start": v(-0.5, -1.13) * mm, "end": v(-0.46, -1.03) * mm});
            skLineSegment(sketch, "E645", {"start": v(-0.46, -1.03) * mm, "end": v(-0.4, -0.94) * mm});
            skLineSegment(sketch, "E646", {"start": v(-0.4, -0.94) * mm, "end": v(-0.3, -0.85) * mm});
            skLineSegment(sketch, "E647", {"start": v(-0.3, -0.85) * mm, "end": v(-0.2, -0.79) * mm});
            skLineSegment(sketch, "E648", {"start": v(-0.2, -0.79) * mm, "end": v(-0.08, -0.75) * mm});
            skLineSegment(sketch, "E649", {"start": v(-0.08, -0.75) * mm, "end": v(0.06, -0.74) * mm});
            skLineSegment(sketch, "E650", {"start": v(0.06, -0.74) * mm, "end": v(0.17, -0.76) * mm});
            skLineSegment(sketch, "E651", {"start": v(0.17, -0.76) * mm, "end": v(0.2, -0.77) * mm});
            skLineSegment(sketch, "E652", {"start": v(0.2, -0.77) * mm, "end": v(0.21, -0.77) * mm});
            skLineSegment(sketch, "E653", {"start": v(0.21, -0.77) * mm, "end": v(0.23, -0.8) * mm});
            skLineSegment(sketch, "E654", {"start": v(0.23, -0.8) * mm, "end": v(0.23, -0.84) * mm});
            skLineSegment(sketch, "E655", {"start": v(0.23, -0.84) * mm, "end": v(0.23, -0.91) * mm});
            skLineSegment(sketch, "E656", {"start": v(0.23, -0.91) * mm, "end": v(0.2, -1) * mm});
            skLineSegment(sketch, "E657", {"start": v(0.2, -1) * mm, "end": v(0.16, -1.07) * mm});
            skLineSegment(sketch, "E658", {"start": v(0.16, -1.07) * mm, "end": v(0.1, -1.16) * mm});
            skLineSegment(sketch, "E659", {"start": v(0.1, -1.16) * mm, "end": v(0.03, -1.24) * mm});
            skLineSegment(sketch, "E660", {"start": v(0.03, -1.24) * mm, "end": v(-0.04, -1.29) * mm});
            skLineSegment(sketch, "E661", {"start": v(-0.04, -1.29) * mm, "end": v(-0.07, -1.3) * mm});
            skLineSegment(sketch, "E662", {"start": v(-0.07, -1.3) * mm, "end": v(-0.09, -1.3) * mm});
            skLineSegment(sketch, "E663", {"start": v(-0.09, -1.3) * mm, "end": v(-0.14, -1.3) * mm});
            skLineSegment(sketch, "E664", {"start": v(-0.14, -1.3) * mm, "end": v(-0.21, -1.31) * mm});
            skLineSegment(sketch, "E665", {"start": v(-0.21, -1.31) * mm, "end": v(-0.3, -1.31) * mm});
            skLineSegment(sketch, "E666", {"start": v(-0.3, -1.31) * mm, "end": v(-0.38, -1.31) * mm});
            skLineSegment(sketch, "E667", {"start": v(-0.38, -1.31) * mm, "end": v(-0.46, -1.3) * mm});
            skLineSegment(sketch, "E668", {"start": v(-0.46, -1.3) * mm, "end": v(-0.51, -1.27) * mm});
            skLineSegment(sketch, "E669", {"start": v(-0.51, -1.27) * mm, "end": v(-0.53, -1.24) * mm});
            skLineSegment(sketch, "E670", {"start": v(-0.53, -1.24) * mm, "end": v(-0.53, -1.23) * mm});
            skLineSegment(sketch, "E671", {"start": v(-1.1, -0.57) * mm, "end": v(-0.9, -0.58) * mm});
            skLineSegment(sketch, "E672", {"start": v(-0.9, -0.58) * mm, "end": v(-0.53, -0.54) * mm});
            skLineSegment(sketch, "E673", {"start": v(-0.53, -0.54) * mm, "end": v(-0.1, -0.47) * mm});
            skLineSegment(sketch, "E674", {"start": v(-0.1, -0.47) * mm, "end": v(0.3, -0.4) * mm});
            skLineSegment(sketch, "E675", {"start": v(0.3, -0.4) * mm, "end": v(0.68, -0.35) * mm});
            skLineSegment(sketch, "E676", {"start": v(0.68, -0.35) * mm, "end": v(1.05, -0.32) * mm});
            skLineSegment(sketch, "E677", {"start": v(1.05, -0.32) * mm, "end": v(1.43, -0.34) * mm});
            skLineSegment(sketch, "E678", {"start": v(1.43, -0.34) * mm, "end": v(1.84, -0.42) * mm});
            skLineSegment(sketch, "E679", {"start": v(1.84, -0.42) * mm, "end": v(2.17, -0.53) * mm});
            skLineSegment(sketch, "E680", {"start": v(2.17, -0.53) * mm, "end": v(2.28, -0.58) * mm});
            skLineSegment(sketch, "E681", {"start": v(-1.17, -0.13) * mm, "end": v(-1.2, -0.16) * mm});
            skLineSegment(sketch, "E682", {"start": v(-1.2, -0.16) * mm, "end": v(-1.33, -0.28) * mm});
            skLineSegment(sketch, "E683", {"start": v(-1.33, -0.28) * mm, "end": v(-1.45, -0.42) * mm});
            skLineSegment(sketch, "E684", {"start": v(-1.45, -0.42) * mm, "end": v(-1.47, -0.45) * mm});
            skLineSegment(sketch, "E685", {"start": v(-1.47, -0.45) * mm, "end": v(-1.36, -0.44) * mm});
            skLineSegment(sketch, "E686", {"start": v(-1.36, -0.44) * mm, "end": v(-0.83, -0.34) * mm});
            skLineSegment(sketch, "E687", {"start": v(-0.83, -0.34) * mm, "end": v(-0.3, -0.16) * mm});
            skLineSegment(sketch, "E688", {"start": v(-0.3, -0.16) * mm, "end": v(-0.2, -0.11) * mm});
            skLineSegment(sketch, "E689", {"start": v(-3, 0.8) * mm, "end": v(-2.91, 0.84) * mm});
            skLineSegment(sketch, "E690", {"start": v(-2.91, 0.84) * mm, "end": v(-2.7, 0.9) * mm});
            skLineSegment(sketch, "E691", {"start": v(-2.7, 0.9) * mm, "end": v(-2.47, 0.96) * mm});
            skLineSegment(sketch, "E692", {"start": v(-2.47, 0.96) * mm, "end": v(-2.28, 1) * mm});
            skLineSegment(sketch, "E693", {"start": v(-2.28, 1) * mm, "end": v(-2.14, 0.98) * mm});
            skLineSegment(sketch, "E694", {"start": v(-2.14, 0.98) * mm, "end": v(-2.04, 0.93) * mm});
            skLineSegment(sketch, "E695", {"start": v(-2.04, 0.93) * mm, "end": v(-2, 0.83) * mm});
            skLineSegment(sketch, "E696", {"start": v(-2, 0.83) * mm, "end": v(-2.03, 0.68) * mm});
            skLineSegment(sketch, "E697", {"start": v(-2.03, 0.68) * mm, "end": v(-2.1, 0.52) * mm});
            skLineSegment(sketch, "E698", {"start": v(-2.1, 0.52) * mm, "end": v(-2.12, 0.47) * mm});
            skLineSegment(sketch, "E699", {"start": v(-3.06, 0.5) * mm, "end": v(-3.03, 0.47) * mm});
            skLineSegment(sketch, "E700", {"start": v(-3.03, 0.47) * mm, "end": v(-2.91, 0.38) * mm});
            skLineSegment(sketch, "E701", {"start": v(-2.91, 0.38) * mm, "end": v(-2.74, 0.3) * mm});
            skLineSegment(sketch, "E702", {"start": v(-2.74, 0.3) * mm, "end": v(-2.55, 0.28) * mm});
            skLineSegment(sketch, "E703", {"start": v(-2.55, 0.28) * mm, "end": v(-2.37, 0.3) * mm});
            skLineSegment(sketch, "E704", {"start": v(-2.37, 0.3) * mm, "end": v(-2.3, 0.32) * mm});
            skLineSegment(sketch, "E705", {"start": v(-2.03, 0.68) * mm, "end": v(-2, 0.69) * mm});
            skLineSegment(sketch, "E706", {"start": v(-2, 0.69) * mm, "end": v(-1.97, 0.69) * mm});
            skLineSegment(sketch, "E707", {"start": v(-1.97, 0.69) * mm, "end": v(-1.86, 0.7) * mm});
            skLineSegment(sketch, "E708", {"start": v(-1.86, 0.7) * mm, "end": v(-1.72, 0.7) * mm});
            skLineSegment(sketch, "E709", {"start": v(-1.72, 0.7) * mm, "end": v(-1.56, 0.71) * mm});
            skLineSegment(sketch, "E710", {"start": v(-1.56, 0.71) * mm, "end": v(-1.4, 0.73) * mm});
            skLineSegment(sketch, "E711", {"start": v(-1.4, 0.73) * mm, "end": v(-1.26, 0.74) * mm});
            skLineSegment(sketch, "E712", {"start": v(-1.26, 0.74) * mm, "end": v(-1.17, 0.74) * mm});
            skLineSegment(sketch, "E713", {"start": v(-1.17, 0.74) * mm, "end": v(-1.14, 0.75) * mm});
            skLineSegment(sketch, "E714", {"start": v(-1.14, 0.75) * mm, "end": v(-1.63, 0.52) * mm});
            skLineSegment(sketch, "E715", {"start": v(-1.63, 0.52) * mm, "end": v(-2.09, 0.52) * mm});
            skLineSegment(sketch, "E716", {"start": v(-2.33, 0.46) * mm, "end": v(-2.32, 0.49) * mm});
            skLineSegment(sketch, "E717", {"start": v(-2.32, 0.49) * mm, "end": v(-2.28, 0.62) * mm});
            skLineSegment(sketch, "E718", {"start": v(-2.28, 0.62) * mm, "end": v(-2.24, 0.75) * mm});
            skLineSegment(sketch, "E719", {"start": v(-2.24, 0.75) * mm, "end": v(-2.22, 0.77) * mm});
            skLineSegment(sketch, "E720", {"start": v(-2.22, 0.77) * mm, "end": v(-2.21, 0.77) * mm});
            skLineSegment(sketch, "E721", {"start": v(-2.21, 0.77) * mm, "end": v(-2.19, 0.78) * mm});
            skLineSegment(sketch, "E722", {"start": v(-2.19, 0.78) * mm, "end": v(-2.16, 0.77) * mm});
            skLineSegment(sketch, "E723", {"start": v(-2.16, 0.77) * mm, "end": v(-2.14, 0.76) * mm});
            skLineSegment(sketch, "E724", {"start": v(-2.14, 0.76) * mm, "end": v(-2.13, 0.74) * mm});
            skLineSegment(sketch, "E725", {"start": v(-2.13, 0.74) * mm, "end": v(-2.13, 0.73) * mm});
            skLineSegment(sketch, "E726", {"start": v(-2.13, 0.73) * mm, "end": v(-2.13, 0.72) * mm});
            skLineSegment(sketch, "E727", {"start": v(-2.13, 0.72) * mm, "end": v(-2.15, 0.7) * mm});
            skLineSegment(sketch, "E728", {"start": v(-2.15, 0.7) * mm, "end": v(-2.18, 0.69) * mm});
            skLineSegment(sketch, "E729", {"start": v(-2.18, 0.69) * mm, "end": v(-2.19, 0.68) * mm});
            skLineSegment(sketch, "E730", {"start": v(-2.19, 0.68) * mm, "end": v(-2.25, 0.55) * mm});
            skLineSegment(sketch, "E731", {"start": v(-2.25, 0.55) * mm, "end": v(-2.24, 0.54) * mm});
            skLineSegment(sketch, "E732", {"start": v(-2.24, 0.54) * mm, "end": v(-2.23, 0.52) * mm});
            skLineSegment(sketch, "E733", {"start": v(-2.23, 0.52) * mm, "end": v(-2.23, 0.5) * mm});
            skLineSegment(sketch, "E734", {"start": v(-2.23, 0.5) * mm, "end": v(-2.23, 0.5) * mm});
            skLineSegment(sketch, "E735", {"start": v(-2.23, 0.5) * mm, "end": v(-2.25, 0.48) * mm});
            skLineSegment(sketch, "E736", {"start": v(-2.25, 0.48) * mm, "end": v(-2.27, 0.47) * mm});
            skLineSegment(sketch, "E737", {"start": v(-2.27, 0.47) * mm, "end": v(-2.28, 0.46) * mm});
            skLineSegment(sketch, "E738", {"start": v(-2.78, 0.4) * mm, "end": v(-2.78, 0.4) * mm});
            skLineSegment(sketch, "E739", {"start": v(-2.78, 0.4) * mm, "end": v(-2.8, 0.4) * mm});
            skLineSegment(sketch, "E740", {"start": v(-2.8, 0.4) * mm, "end": v(-2.83, 0.41) * mm});
            skLineSegment(sketch, "E741", {"start": v(-2.83, 0.41) * mm, "end": v(-2.87, 0.44) * mm});
            skLineSegment(sketch, "E742", {"start": v(-2.87, 0.44) * mm, "end": v(-2.91, 0.48) * mm});
            skLineSegment(sketch, "E743", {"start": v(-2.91, 0.48) * mm, "end": v(-2.95, 0.53) * mm});
            skLineSegment(sketch, "E744", {"start": v(-2.95, 0.53) * mm, "end": v(-2.98, 0.58) * mm});
            skLineSegment(sketch, "E745", {"start": v(-2.98, 0.58) * mm, "end": v(-2.99, 0.63) * mm});
            skLineSegment(sketch, "E746", {"start": v(-2.99, 0.63) * mm, "end": v(-2.99, 0.67) * mm});
            skLineSegment(sketch, "E747", {"start": v(-2.99, 0.67) * mm, "end": v(-2.98, 0.68) * mm});
            skLineSegment(sketch, "E748", {"start": v(-2.98, 0.68) * mm, "end": v(-2.98, 0.69) * mm});
            skLineSegment(sketch, "E749", {"start": v(-2.98, 0.69) * mm, "end": v(-2.96, 0.71) * mm});
            skLineSegment(sketch, "E750", {"start": v(-2.96, 0.71) * mm, "end": v(-2.9, 0.75) * mm});
            skLineSegment(sketch, "E751", {"start": v(-2.9, 0.75) * mm, "end": v(-2.85, 0.78) * mm});
            skLineSegment(sketch, "E752", {"start": v(-2.85, 0.78) * mm, "end": v(-2.78, 0.8) * mm});
            skLineSegment(sketch, "E753", {"start": v(-2.78, 0.8) * mm, "end": v(-2.71, 0.82) * mm});
            skLineSegment(sketch, "E754", {"start": v(-2.71, 0.82) * mm, "end": v(-2.66, 0.83) * mm});
            skLineSegment(sketch, "E755", {"start": v(-2.66, 0.83) * mm, "end": v(-2.62, 0.83) * mm});
            skLineSegment(sketch, "E756", {"start": v(-2.62, 0.83) * mm, "end": v(-2.6, 0.82) * mm});
            skLineSegment(sketch, "E757", {"start": v(-2.6, 0.82) * mm, "end": v(-2.6, 0.82) * mm});
            skLineSegment(sketch, "E758", {"start": v(-2.6, 0.82) * mm, "end": v(-2.61, 0.78) * mm});
            skLineSegment(sketch, "E759", {"start": v(-2.61, 0.78) * mm, "end": v(-2.67, 0.61) * mm});
            skLineSegment(sketch, "E760", {"start": v(-2.67, 0.61) * mm, "end": v(-2.76, 0.44) * mm});
            skLineSegment(sketch, "E761", {"start": v(-2.76, 0.44) * mm, "end": v(-2.78, 0.4) * mm});
            skLineSegment(sketch, "E762", {"start": v(-2.32, -0.14) * mm, "end": v(-2.31, -0.15) * mm});
            skLineSegment(sketch, "E763", {"start": v(-2.31, -0.15) * mm, "end": v(-2.2, -0.25) * mm});
            skLineSegment(sketch, "E764", {"start": v(-2.2, -0.25) * mm, "end": v(-2.11, -0.37) * mm});
            skLineSegment(sketch, "E765", {"start": v(-2.11, -0.37) * mm, "end": v(-2.1, -0.4) * mm});
            skLineSegment(sketch, "E766", {"start": v(-2.1, -0.4) * mm, "end": v(-2.12, -0.43) * mm});
            skLineSegment(sketch, "E767", {"start": v(-2.12, -0.43) * mm, "end": v(-2.22, -0.54) * mm});
            skLineSegment(sketch, "E768", {"start": v(-2.22, -0.54) * mm, "end": v(-2.37, -0.64) * mm});
            skLineSegment(sketch, "E769", {"start": v(-2.37, -0.64) * mm, "end": v(-2.55, -0.7) * mm});
            skLineSegment(sketch, "E770", {"start": v(-2.55, -0.7) * mm, "end": v(-2.7, -0.72) * mm});
            skLineSegment(sketch, "E771", {"start": v(-2.7, -0.72) * mm, "end": v(-2.8, -0.7) * mm});
            skLineSegment(sketch, "E772", {"start": v(-2.32, -0.14) * mm, "end": v(-2.3, -0.17) * mm});
            skLineSegment(sketch, "E773", {"start": v(-2.3, -0.17) * mm, "end": v(-2.18, -0.46) * mm});
            skLineSegment(sketch, "E774", {"start": v(-2.18, -0.46) * mm, "end": v(-2.17, -0.48) * mm});
            skLineSegment(sketch, "E775", {"start": v(1.14, 0.3) * mm, "end": v(1.23, 0.31) * mm});
            skLineSegment(sketch, "E776", {"start": v(-2.15, -0.66) * mm, "end": v(-2.19, -0.66) * mm});
            skLineSegment(sketch, "E777", {"start": v(-2.19, -0.66) * mm, "end": v(-2.3, -0.69) * mm});
            skLineSegment(sketch, "E778", {"start": v(-2.3, -0.69) * mm, "end": v(-2.42, -0.72) * mm});
            skLineSegment(sketch, "E779", {"start": v(-2.42, -0.72) * mm, "end": v(-2.5, -0.76) * mm});
            skLineSegment(sketch, "E780", {"start": v(-2.5, -0.76) * mm, "end": v(-2.53, -0.8) * mm});
            skLineSegment(sketch, "E781", {"start": v(-2.53, -0.8) * mm, "end": v(-2.53, -0.83) * mm});
            skLineSegment(sketch, "E782", {"start": v(-2.53, -0.83) * mm, "end": v(-2.49, -0.86) * mm});
            skLineSegment(sketch, "E783", {"start": v(-2.49, -0.86) * mm, "end": v(-2.41, -0.88) * mm});
            skLineSegment(sketch, "E784", {"start": v(-2.41, -0.88) * mm, "end": v(-2.34, -0.88) * mm});
            skLineSegment(sketch, "E785", {"start": v(-2.34, -0.88) * mm, "end": v(-2.31, -0.88) * mm});
            skLineSegment(sketch, "E786", {"start": v(-2.31, -0.88) * mm, "end": v(-2.33, -0.88) * mm});
            skLineSegment(sketch, "E787", {"start": v(-2.33, -0.88) * mm, "end": v(-2.4, -0.89) * mm});
            skLineSegment(sketch, "E788", {"start": v(-2.4, -0.89) * mm, "end": v(-2.46, -0.9) * mm});
            skLineSegment(sketch, "E789", {"start": v(-2.46, -0.9) * mm, "end": v(-2.53, -0.94) * mm});
            skLineSegment(sketch, "E790", {"start": v(-2.53, -0.94) * mm, "end": v(-2.57, -0.97) * mm});
            skLineSegment(sketch, "E791", {"start": v(-2.57, -0.97) * mm, "end": v(-2.58, -0.98) * mm});
            skLineSegment(sketch, "E792", {"start": v(-2.58, -0.98) * mm, "end": v(-2.59, -0.99) * mm});
            skLineSegment(sketch, "E793", {"start": v(-2.59, -0.99) * mm, "end": v(-2.58, -1) * mm});
            skLineSegment(sketch, "E794", {"start": v(-2.58, -1) * mm, "end": v(-2.54, -1.02) * mm});
            skLineSegment(sketch, "E795", {"start": v(-2.54, -1.02) * mm, "end": v(-2.48, -1.03) * mm});
            skLineSegment(sketch, "E796", {"start": v(-2.48, -1.03) * mm, "end": v(-2.42, -1.04) * mm});
            skLineSegment(sketch, "E797", {"start": v(-2.42, -1.04) * mm, "end": v(-2.4, -1.04) * mm});
            skLineSegment(sketch, "E798", {"start": v(-2.4, -1.04) * mm, "end": v(-2.42, -1.04) * mm});
            skLineSegment(sketch, "E799", {"start": v(-2.42, -1.04) * mm, "end": v(-2.51, -1.06) * mm});
            skLineSegment(sketch, "E800", {"start": v(-2.51, -1.06) * mm, "end": v(-2.6, -1.1) * mm});
            skLineSegment(sketch, "E801", {"start": v(-2.6, -1.1) * mm, "end": v(-2.61, -1.12) * mm});
            skLineSegment(sketch, "E802", {"start": v(-0.04, -0.87) * mm, "end": v(-0.06, -0.88) * mm});
            skLineSegment(sketch, "E803", {"start": v(-0.06, -0.88) * mm, "end": v(-0.12, -0.92) * mm});
            skLineSegment(sketch, "E804", {"start": v(-0.12, -0.92) * mm, "end": v(-0.17, -0.99) * mm});
            skLineSegment(sketch, "E805", {"start": v(-0.17, -0.99) * mm, "end": v(-0.2, -1.07) * mm});
            skLineSegment(sketch, "E806", {"start": v(-0.2, -1.07) * mm, "end": v(-0.22, -1.13) * mm});
            skLineSegment(sketch, "E807", {"start": v(-0.22, -1.13) * mm, "end": v(-0.23, -1.15) * mm});
            skLineSegment(sketch, "E808", {"start": v(-0.23, -1.15) * mm, "end": v(-0.22, -1.14) * mm});
            skLineSegment(sketch, "E809", {"start": v(-0.22, -1.14) * mm, "end": v(-0.2, -1.13) * mm});
            skLineSegment(sketch, "E810", {"start": v(-0.2, -1.13) * mm, "end": v(-0.16, -1.1) * mm});
            skLineSegment(sketch, "E811", {"start": v(-0.16, -1.1) * mm, "end": v(-0.12, -1.08) * mm});
            skLineSegment(sketch, "E812", {"start": v(-0.12, -1.08) * mm, "end": v(-0.1, -1.04) * mm});
            skLineSegment(sketch, "E813", {"start": v(-0.1, -1.04) * mm, "end": v(-0.06, -1) * mm});
            skLineSegment(sketch, "E814", {"start": v(-0.06, -1) * mm, "end": v(-0.05, -0.95) * mm});
            skLineSegment(sketch, "E815", {"start": v(-0.05, -0.95) * mm, "end": v(-0.04, -0.9) * mm});
            skLineSegment(sketch, "E816", {"start": v(-0.04, -0.9) * mm, "end": v(-0.04, -0.88) * mm});
            skLineSegment(sketch, "E817", {"start": v(-0.04, -0.88) * mm, "end": v(-0.04, -0.87) * mm});
            skLineSegment(sketch, "E818.bottom", {"start": v(-7.5, 3.5) * mm, "end": v(7.5, 3.5) * mm});
            skLineSegment(sketch, "E818.top", {"start": v(-7.5, -3.5) * mm, "end": v(7.5, -3.5) * mm});
            skLineSegment(sketch, "E818.left", {"start": v(-7.5, 3.5) * mm, "end": v(-7.5, -3.5) * mm});
            skLineSegment(sketch, "E818.right", {"start": v(7.5, 3.5) * mm, "end": v(7.5, -3.5) * mm});
            skPoint(sketch, "E818.middle", {"position": v(0, 0) * mm});
            skLineSegment(sketch, "E819", {"start": v(-3, 0.8) * mm, "end": v(-2.99, 0.84) * mm});
            skLineSegment(sketch, "E820", {"start": v(-3.06, 0.5) * mm, "end": v(-3.07, 0.53) * mm});
            skLineSegment(sketch, "E821", {"start": v(-2.33, 0.46) * mm, "end": v(-2.28, 0.46) * mm});
            skLineSegment(sketch, "E822", {"start": v(-2.12, 0.47) * mm, "end": v(-2.12, 0.46) * mm});
            skLineSegment(sketch, "E823", {"start": v(-2.32, -0.14) * mm, "end": v(-2.34, -0.12) * mm});
            skLineSegment(sketch, "E824", {"start": v(-2.2, -0.54) * mm, "end": v(-2.22, -0.54) * mm});
            skSolve(sketch);
        }
        {
            var Q0;
            Q0=makeQuery(id+"F0.imprint","IMPRINT",FACE,{"disambiguationData":[TD([[makeQuery(id+"F0.imprint","IMPRINT",EDGE,{"derivedFrom":sQuery(id+"F0.wireOp",EDGE,"E180")}),-1.0]])]});
            var Q1;
            Q1=makeQuery(id+"F0.imprint","IMPRINT",FACE,{"disambiguationData":[TD([[makeQuery(id+"F0.imprint","IMPRINT",EDGE,{"derivedFrom":sQuery(id+"F0.wireOp",EDGE,"E243")}),1.0]])]});
            var Q2;
            Q2=makeQuery(id+"F0.imprint","IMPRINT",FACE,{"disambiguationData":[TD([[makeQuery(id+"F0.imprint","IMPRINT",EDGE,{"derivedFrom":sQuery(id+"F0.wireOp",EDGE,"E298")}),1.0]])]});
            var Q3;
            Q3=makeQuery(id+"F0.imprint","IMPRINT",FACE,{"disambiguationData":[TD([[makeQuery(id+"F0.imprint","IMPRINT",EDGE,{"derivedFrom":sQuery(id+"F0.wireOp",EDGE,"E344")}),1.0]])]});
            var Q4;
            Q4=makeQuery(id+"F0.imprint","IMPRINT",FACE,{"disambiguationData":[TD([[makeQuery(id+"F0.imprint","IMPRINT",EDGE,{"derivedFrom":sQuery(id+"F0.wireOp",EDGE,"E372")}),1.0]])]});
            var Q5;
            Q5=makeQuery(id+"F0.imprint","IMPRINT",FACE,{"disambiguationData":[TD([[makeQuery(id+"F0.imprint","IMPRINT",EDGE,{"derivedFrom":sQuery(id+"F0.wireOp",EDGE,"E430")}),-1.0]])]});
            var Q6;
            Q6=makeQuery(id+"F0.imprint","IMPRINT",FACE,{"disambiguationData":[TD([[makeQuery(id+"F0.imprint","IMPRINT",EDGE,{"derivedFrom":sQuery(id+"F0.wireOp",EDGE,"E488")}),-1.0]])]});
            var Q7;
            Q7=makeQuery(id+"F0.imprint","IMPRINT",FACE,{"disambiguationData":[TD([[makeQuery(id+"F0.imprint","IMPRINT",EDGE,{"derivedFrom":sQuery(id+"F0.wireOp",EDGE,"E516")}),1.0]])]});
            var Q8;
            Q8=makeQuery(id+"F0.imprint","IMPRINT",FACE,{"disambiguationData":[TD([[makeQuery(id+"F0.imprint","IMPRINT",EDGE,{"derivedFrom":sQuery(id+"F0.wireOp",EDGE,"E642")}),-1.0]])]});
            var Q9;
            Q9=makeQuery(id+"F0.imprint","IMPRINT",FACE,{"disambiguationData":[TD([[makeQuery(id+"F0.imprint","IMPRINT",EDGE,{"derivedFrom":sQuery(id+"F0.wireOp",EDGE,"E624")}),-1.0]])]});
            extrude(context, id + "F1", {"entities" : qUnion([Q0, Q1, Q2, Q3, Q4, Q5, Q6, Q7, Q8, Q9]), "depth" : 2 * mm, "offsetDistance" : 25 * mm});
        }
        {
            var Q0;
            Q0=makeQuery(id+"F0.imprint","IMPRINT",FACE,{"disambiguationData":[TD([[makeQuery(id+"F0.imprint","IMPRINT",EDGE,{"derivedFrom":sQuery(id+"F0.wireOp",EDGE,"E0")}),-1.0]])]});
            var Q1;
            Q1=makeQuery(id+"F0.imprint","IMPRINT",FACE,{"disambiguationData":[TD([[makeQuery(id+"F0.imprint","IMPRINT",EDGE,{"derivedFrom":sQuery(id+"F0.wireOp",EDGE,"E9")}),-1.0]])]});
            extrude(context, id + "F2", {"entities" : qUnion([Q0, Q1]), "depth" : 1.8 * mm, "offsetDistance" : 25 * mm});
        }
        {
            var Q0;
            Q0=makeQuery(id+"F0.imprint","IMPRINT",FACE,{"disambiguationData":[TD([[makeQuery(id+"F0.imprint","IMPRINT",EDGE,{"derivedFrom":sQuery(id+"F0.wireOp",EDGE,"E738")}),-1.0]])]});
            extrude(context, id + "F3", {"entities" : qUnion([Q0]), "operationType" : NewBodyOperationType.ADD, "depth" : 1.7 * mm, "offsetDistance" : 25 * mm});
        }
        {
            var Q0;
            Q0=makeQuery(id+"F0.imprint","IMPRINT",FACE,{"disambiguationData":[TD([[makeQuery(id+"F0.imprint","IMPRINT",EDGE,{"derivedFrom":sQuery(id+"F0.wireOp",EDGE,"E7")}),-1.0]])]});
            extrude(context, id + "F4", {"entities" : qUnion([Q0]), "depth" : 1.8 * mm, "offsetDistance" : 25 * mm});
        }
        {
            var Q0;
            Q0=makeQuery(id+"F1.opExtrude","SWEPT_BODY",BODY,{"disambiguationData":[OSD([sQuery(id+"F0.wireOp",EDGE,"E372"),sQuery(id+"F0.wireOp",EDGE,"E373"),sQuery(id+"F0.wireOp",EDGE,"E374"),sQuery(id+"F0.wireOp",EDGE,"E375"),sQuery(id+"F0.wireOp",EDGE,"E376"),sQuery(id+"F0.wireOp",EDGE,"E377"),sQuery(id+"F0.wireOp",EDGE,"E378"),sQuery(id+"F0.wireOp",EDGE,"E379"),sQuery(id+"F0.wireOp",EDGE,"E380"),sQuery(id+"F0.wireOp",EDGE,"E381"),sQuery(id+"F0.wireOp",EDGE,"E382"),sQuery(id+"F0.wireOp",EDGE,"E383"),sQuery(id+"F0.wireOp",EDGE,"E384"),sQuery(id+"F0.wireOp",EDGE,"E385"),sQuery(id+"F0.wireOp",EDGE,"E386"),sQuery(id+"F0.wireOp",EDGE,"E387"),sQuery(id+"F0.wireOp",EDGE,"E388"),sQuery(id+"F0.wireOp",EDGE,"E389"),sQuery(id+"F0.wireOp",EDGE,"E390"),sQuery(id+"F0.wireOp",EDGE,"E391"),sQuery(id+"F0.wireOp",EDGE,"E392"),sQuery(id+"F0.wireOp",EDGE,"E393"),sQuery(id+"F0.wireOp",EDGE,"E394"),sQuery(id+"F0.wireOp",EDGE,"E395"),sQuery(id+"F0.wireOp",EDGE,"E396"),sQuery(id+"F0.wireOp",EDGE,"E397"),sQuery(id+"F0.wireOp",EDGE,"E398"),sQuery(id+"F0.wireOp",EDGE,"E399"),sQuery(id+"F0.wireOp",EDGE,"E400"),sQuery(id+"F0.wireOp",EDGE,"E401"),sQuery(id+"F0.wireOp",EDGE,"E402"),sQuery(id+"F0.wireOp",EDGE,"E403"),sQuery(id+"F0.wireOp",EDGE,"E404"),sQuery(id+"F0.wireOp",EDGE,"E405"),sQuery(id+"F0.wireOp",EDGE,"E406"),sQuery(id+"F0.wireOp",EDGE,"E407"),sQuery(id+"F0.wireOp",EDGE,"E408"),sQuery(id+"F0.wireOp",EDGE,"E409"),sQuery(id+"F0.wireOp",EDGE,"E410"),sQuery(id+"F0.wireOp",EDGE,"E411"),sQuery(id+"F0.wireOp",EDGE,"E412"),sQuery(id+"F0.wireOp",EDGE,"E413"),sQuery(id+"F0.wireOp",EDGE,"E414"),sQuery(id+"F0.wireOp",EDGE,"E415"),sQuery(id+"F0.wireOp",EDGE,"E416"),sQuery(id+"F0.wireOp",EDGE,"E417"),sQuery(id+"F0.wireOp",EDGE,"E418"),sQuery(id+"F0.wireOp",EDGE,"E419"),sQuery(id+"F0.wireOp",EDGE,"E420"),sQuery(id+"F0.wireOp",EDGE,"E421"),sQuery(id+"F0.wireOp",EDGE,"E422"),sQuery(id+"F0.wireOp",EDGE,"E423"),sQuery(id+"F0.wireOp",EDGE,"E424"),sQuery(id+"F0.wireOp",EDGE,"E425"),sQuery(id+"F0.wireOp",EDGE,"E426"),sQuery(id+"F0.wireOp",EDGE,"E427"),sQuery(id+"F0.wireOp",EDGE,"E428"),sQuery(id+"F0.wireOp",EDGE,"E429")])]});
            var Q1;
            Q1=sQuery(id+"F0.wireOp",VERTEX,"E818.middle");
            transform(context, id + "F5", {"entities" : qUnion([Q0]), "transformType" : TransformType.SCALE_UNIFORMLY, "scale" : 2, "scalePoint" : qUnion([Q1]), "makeCopy" : false});
        }
    });
